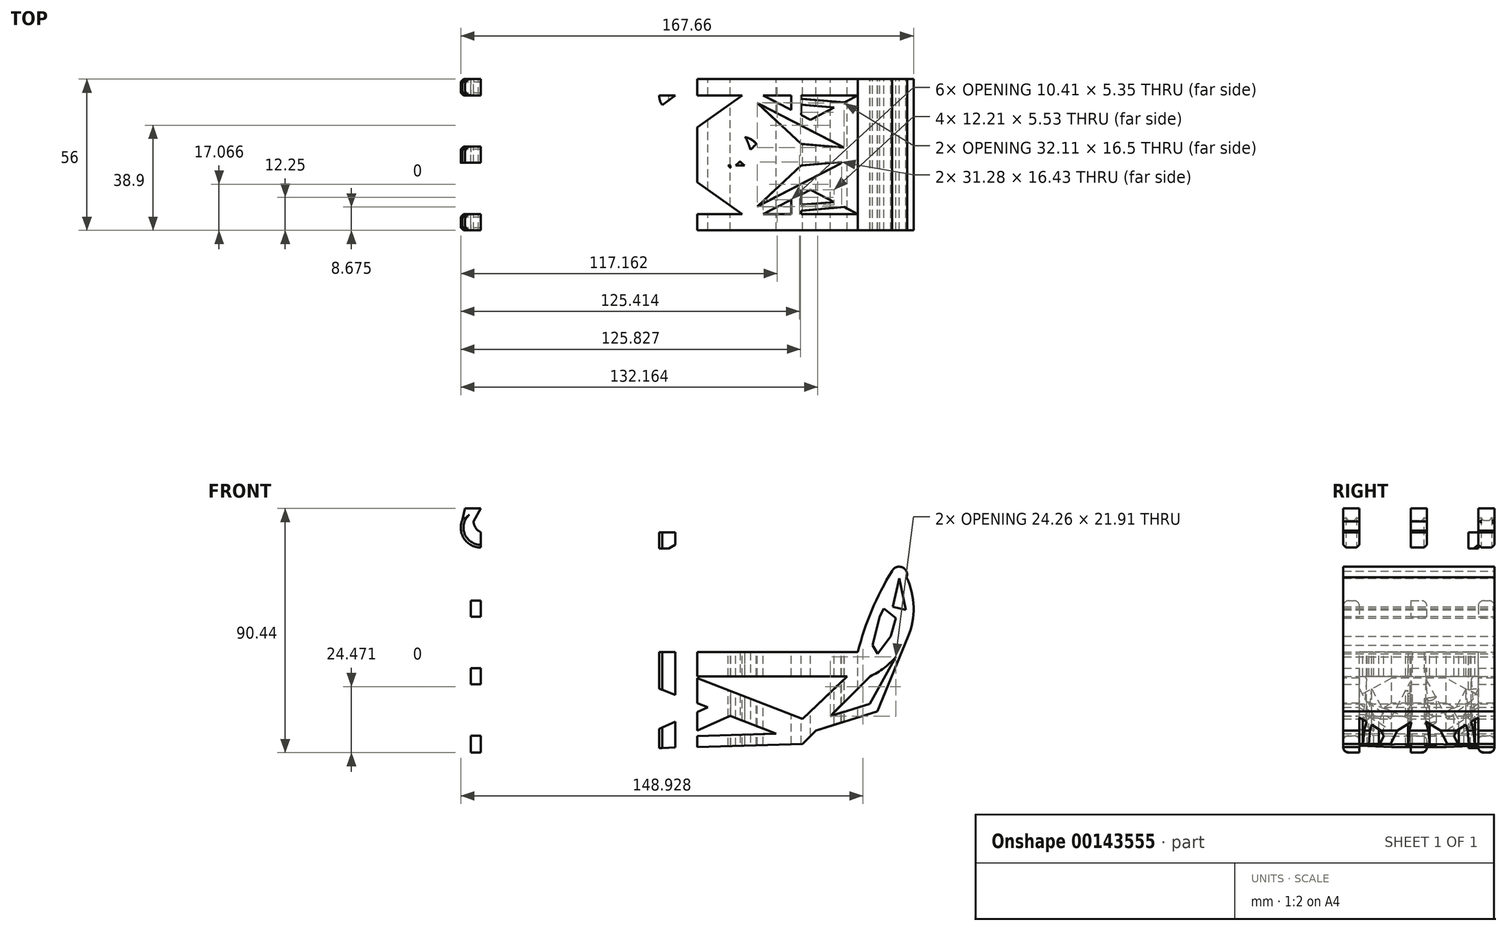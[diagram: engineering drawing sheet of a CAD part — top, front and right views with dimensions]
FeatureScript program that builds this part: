
annotation { "Feature Type Name" : "Feature", "Feature Type Description" : "" }
export const myFeature = defineFeature(function(context is Context, id is Id, definition is map)
    precondition{}
    {
        {
            var Q0;
            Q0=qCreatedBy(makeId("Front.planeOp"),FACE);
            var sketch = newSketch(context, id + "F0", { "sketchPlane" : qUnion([Q0])});
            skLineSegment(sketch, "E0.bottom", {"start": v(0, 0) * mm, "end": v(2.2, 0) * mm});
            skLineSegment(sketch, "E0.top", {"start": v(0, 6) * mm, "end": v(2.2, 6) * mm});
            skLineSegment(sketch, "E0.left", {"start": v(0, 0) * mm, "end": v(0, 6) * mm});
            skLineSegment(sketch, "E1.bottom", {"start": v(0, 6) * mm, "end": v(-4.66, 6) * mm});
            skLineSegment(sketch, "E1.top", {"start": v(0, 0.4) * mm, "end": v(-4.66, 0.4) * mm});
            skLineSegment(sketch, "E1.left", {"start": v(0, 6) * mm, "end": v(0, 0.4) * mm});
            skLineSegment(sketch, "E1.right", {"start": v(-4.66, 6) * mm, "end": v(-4.66, 0.4) * mm});
            skArc(sketch, "E2", {"start": v(-7.33, 10.05) * mm, "mid": v(-6.52, 7.68) * mm, "end": v(-4.66, 6) * mm});
            skArc(sketch, "E3", {"start": v(-11.52, 10.48) * mm, "mid": v(-10.76, 3.63) * mm, "end": v(-4.66, 0.4) * mm});
            skLineSegment(sketch, "E4", {"start": v(-4.66, 14.86) * mm, "end": v(-10.43, 14.86) * mm});
            skLineSegment(sketch, "E5", {"start": v(-10.43, 14.86) * mm, "end": v(-12, 8.6) * mm});
            skLineSegment(sketch, "E6", {"start": v(-4.66, 14.86) * mm, "end": v(-7.33, 10.05) * mm});
            skLineSegment(sketch, "E7", {"start": v(-8.25, 8.4) * mm, "end": v(-4.66, 6) * mm});
            skLineSegment(sketch, "E8.bottom", {"start": v(0, 6) * mm, "end": v(8, 6) * mm});
            skLineSegment(sketch, "E8.left", {"start": v(0, 6) * mm, "end": v(0, -7.26) * mm});
            skLineSegment(sketch, "E8.right", {"start": v(8, 6) * mm, "end": v(8, -7.26) * mm});
            skPoint(sketch, "E9.startSnap0", {"position": v(8, -0.63) * mm});
            skLineSegment(sketch, "E10.left", {"start": v(0, -7.26) * mm, "end": v(0, -22.3) * mm});
            skLineSegment(sketch, "E11", {"start": v(0, 3.2) * mm, "end": v(0, -22.3) * mm, "construction": true});
            skLineSegment(sketch, "E12.bottom", {"start": v(-8.37, -19.3) * mm, "end": v(0, -19.3) * mm});
            skLineSegment(sketch, "E12.top", {"start": v(-8.37, -25.3) * mm, "end": v(8, -25.3) * mm});
            skLineSegment(sketch, "E12.left", {"start": v(-8.37, -19.3) * mm, "end": v(-8.37, -25.3) * mm});
            skPoint(sketch, "E12.middle", {"position": v(0, -22.3) * mm});
            skLineSegment(sketch, "E13", {"start": v(8, -7.26) * mm, "end": v(8, -25.3) * mm});
            skLineSegment(sketch, "E14", {"start": v(0, -25.3) * mm, "end": v(-8.37, -25.3) * mm});
            skPoint(sketch, "E12.right.start.orphan", {"position": v(8.37, -19.3) * mm});
            skPoint(sketch, "E15.orphan", {"position": v(8.37, -25.3) * mm});
            skPoint(sketch, "E9.start.orphan", {"position": v(8, 0) * mm});
            skPoint(sketch, "E16.start.orphan", {"position": v(37.05, 0) * mm});
            skLineSegment(sketch, "E17.top", {"start": v(0, -47.3) * mm, "end": v(0.27, -47.3) * mm});
            skLineSegment(sketch, "E17.left", {"start": v(0, -22.3) * mm, "end": v(0, -38.12) * mm});
            skLineSegment(sketch, "E17.right", {"start": v(8, -22.3) * mm, "end": v(8, -38.33) * mm});
            skLineSegment(sketch, "E18.bottom", {"start": v(-8.37, -44.3) * mm, "end": v(0.18, -44.3) * mm});
            skLineSegment(sketch, "E18.top", {"start": v(-8.37, -50.3) * mm, "end": v(0.36, -50.3) * mm});
            skLineSegment(sketch, "E18.left", {"start": v(-8.37, -44.3) * mm, "end": v(-8.37, -50.3) * mm});
            skLineSegment(sketch, "E18.right", {"start": v(8.37, -47.3) * mm, "end": v(8.37, -47.46) * mm});
            skPoint(sketch, "E18.middle", {"position": v(0, -47.3) * mm});
            skLineSegment(sketch, "E19.bottom", {"start": v(8.37, -44.3) * mm, "end": v(8, -44.3) * mm});
            skLineSegment(sketch, "E19.top", {"start": v(0.36, -50.3) * mm, "end": v(-8.37, -50.3) * mm});
            skPoint(sketch, "E19.middle", {"position": v(8, -47.3) * mm});
            skPoint(sketch, "E19.right.end.orphan", {"position": v(-128, -50.3) * mm});
            skPoint(sketch, "E19.right.start.orphan", {"position": v(-119, -44.3) * mm});
            skLineSegment(sketch, "E20.bottom", {"start": v(0, 6) * mm, "end": v(75.48, 6) * mm});
            skLineSegment(sketch, "E20.left", {"start": v(0, 6) * mm, "end": v(0, 0) * mm});
            skLineSegment(sketch, "E21.bottom", {"start": v(8, -38.33) * mm, "end": v(133.63, -38.33) * mm});
            skLineSegment(sketch, "E21.left", {"start": v(8, -36.1) * mm, "end": v(8, -38.33) * mm});
            skLineSegment(sketch, "E22.bottom", {"start": v(8, -38.33) * mm, "end": v(135, -38.33) * mm});
            skLineSegment(sketch, "E22.top", {"start": v(8, -47.3) * mm, "end": v(8.37, -47.3) * mm});
            skPoint(sketch, "E23.endSnap0", {"position": v(4, -47.3) * mm});
            skLineSegment(sketch, "E24", {"start": v(4, -47.3) * mm, "end": v(4, -50.3) * mm});
            skLineSegment(sketch, "E25", {"start": v(139.5, -47.3) * mm, "end": v(114.54, -72.3) * mm});
            skLineSegment(sketch, "E26", {"start": v(104.76, -68.54) * mm, "end": v(87.68, -61.97) * mm});
            skLineSegment(sketch, "E27", {"start": v(131.03, -47.3) * mm, "end": v(114.54, -63.04) * mm});
            skLineSegment(sketch, "E28", {"start": v(114.54, -63.04) * mm, "end": v(73.6, -47.3) * mm});
            skPoint(sketch, "E29.centerSnap0", {"position": v(4, -59.8) * mm});
            skLineSegment(sketch, "E30", {"start": v(17.34, -47.3) * mm, "end": v(10.24, -53.9) * mm});
            skLineSegment(sketch, "E31", {"start": v(10.24, -53.9) * mm, "end": v(10.24, -64.47) * mm});
            skLineSegment(sketch, "E32", {"start": v(10.24, -64.47) * mm, "end": v(15, -66.9) * mm});
            skLineSegment(sketch, "E33", {"start": v(15, -66.9) * mm, "end": v(27.64, -60.68) * mm});
            skLineSegment(sketch, "E34.bottom", {"start": v(-4.5, -69.3) * mm, "end": v(4, -69.3) * mm});
            skLineSegment(sketch, "E34.top", {"start": v(-4.5, -75.3) * mm, "end": v(12.5, -75.3) * mm});
            skPoint(sketch, "E34.middle", {"position": v(4, -72.3) * mm});
            skLineSegment(sketch, "E35", {"start": v(21.25, -71) * mm, "end": v(36.6, -63.46) * mm});
            skLineSegment(sketch, "E36", {"start": v(12.5, -75.3) * mm, "end": v(114.54, -72.3) * mm});
            skPoint(sketch, "E37.end.orphan", {"position": v(4, -77.18) * mm});
            skLineSegment(sketch, "E38", {"start": v(21.25, -71) * mm, "end": v(52.02, -70.1) * mm});
            skPoint(sketch, "E39.orphan", {"position": v(135, -50.3) * mm});
            skPoint(sketch, "E19.left.start.orphan", {"position": v(144, -44.3) * mm});
            skLineSegment(sketch, "E40.trimOffspring", {"start": v(73.6, -47.3) * mm, "end": v(131.03, -47.3) * mm});
            skLineSegment(sketch, "E41", {"start": v(51.94, -55.92) * mm, "end": v(60.4, -51.48) * mm});
            skLineSegment(sketch, "E42", {"start": v(52.53, -48.45) * mm, "end": v(21.76, -47.45) * mm});
            skLineSegment(sketch, "E43", {"start": v(8.37, -47.46) * mm, "end": v(8, -47.3) * mm});
            skLineSegment(sketch, "E44", {"start": v(36.6, -63.46) * mm, "end": v(52.02, -70.1) * mm});
            skLineSegment(sketch, "E45", {"start": v(70.6, -69.54) * mm, "end": v(87.68, -61.97) * mm});
            skLineSegment(sketch, "E46", {"start": v(79.42, -58.8) * mm, "end": v(60.4, -67.23) * mm});
            skLineSegment(sketch, "E47", {"start": v(60.4, -67.23) * mm, "end": v(43.62, -60) * mm});
            skLineSegment(sketch, "E48.trimOffspring", {"start": v(43.62, -60) * mm, "end": v(51.94, -55.92) * mm});
            skPoint(sketch, "E49.end.orphan", {"position": v(60.4, -69.84) * mm});
            skPoint(sketch, "E49.start.orphan", {"position": v(82.58, -60.01) * mm});
            skLineSegment(sketch, "E50.trimOffspring", {"start": v(70.6, -69.54) * mm, "end": v(104.76, -68.54) * mm});
            skPoint(sketch, "E29.center.orphan", {"position": v(17.34, -59.8) * mm});
            skPoint(sketch, "E51.start.orphan", {"position": v(13.8, -50.6) * mm});
            skLineSegment(sketch, "E52", {"start": v(17.34, -47.3) * mm, "end": v(27.64, -60.68) * mm});
            skLineSegment(sketch, "E53", {"start": v(36.48, -56.34) * mm, "end": v(40.82, -54.2) * mm});
            skLineSegment(sketch, "E54", {"start": v(21.76, -47.45) * mm, "end": v(36.48, -56.34) * mm});
            skLineSegment(sketch, "E55.trimOffspring", {"start": v(36.48, -56.34) * mm, "end": v(52.53, -48.45) * mm});
            skArc(sketch, "E56", {"start": v(147.62, -8.33) * mm, "mid": v(140.11, -22.82) * mm, "end": v(135, -38.33) * mm});
            skArc(sketch, "E57", {"start": v(139.5, -47.3) * mm, "mid": v(144.65, -44.25) * mm, "end": v(149.02, -40.15) * mm});
            skArc(sketch, "E58", {"start": v(153.03, -10.64) * mm, "mid": v(151.41, -6.95) * mm, "end": v(147.62, -8.33) * mm});
            skLineSegment(sketch, "E59", {"start": v(150.25, -11.01) * mm, "end": v(152.71, -22.66) * mm});
            skLineSegment(sketch, "E60", {"start": v(147.92, -21.6) * mm, "end": v(152.71, -22.66) * mm});
            skLineSegment(sketch, "E61.trimOffspring", {"start": v(147.92, -21.6) * mm, "end": v(150.25, -11.01) * mm});
            skLineSegment(sketch, "E62", {"start": v(149.02, -40.15) * mm, "end": v(139.32, -57.51) * mm});
            skLineSegment(sketch, "E63", {"start": v(139.32, -57.51) * mm, "end": v(124.76, -62.06) * mm});
            skLineSegment(sketch, "E64", {"start": v(124.76, -62.06) * mm, "end": v(119.44, -67.4) * mm});
            skLineSegment(sketch, "E65", {"start": v(119.44, -67.4) * mm, "end": v(142.16, -60.29) * mm});
            skLineSegment(sketch, "E66", {"start": v(142.16, -60.29) * mm, "end": v(153.54, -32.79) * mm});
            skArc(sketch, "E67.trimOffspring", {"start": v(153.54, -32.79) * mm, "mid": v(155.61, -21.66) * mm, "end": v(153.03, -10.64) * mm});
            skLineSegment(sketch, "E68", {"start": v(143.06, -25.11) * mm, "end": v(140.34, -35.8) * mm});
            skLineSegment(sketch, "E69", {"start": v(140.34, -35.8) * mm, "end": v(142.29, -38.91) * mm});
            skLineSegment(sketch, "E70", {"start": v(142.29, -38.91) * mm, "end": v(147.14, -32.5) * mm});
            skLineSegment(sketch, "E71", {"start": v(147.14, -32.5) * mm, "end": v(149.09, -25.7) * mm});
            skLineSegment(sketch, "E72", {"start": v(149.09, -25.7) * mm, "end": v(144.62, -22.2) * mm});
            skLineSegment(sketch, "E73", {"start": v(144.62, -22.2) * mm, "end": v(143.06, -25.11) * mm});
            skPoint(sketch, "E20.right.end.orphan", {"position": v(129.94, 0) * mm});
            skLineSegment(sketch, "E74.trimOffspring", {"start": v(79.42, -58.8) * mm, "end": v(60.4, -51.48) * mm});
            skPoint(sketch, "E34.right.start.orphan", {"position": v(12.5, -69.3) * mm});
            skLineSegment(sketch, "E75", {"start": v(0, -38.12) * mm, "end": v(0.18, -44.3) * mm});
            skLineSegment(sketch, "E76", {"start": v(1.1, -75.3) * mm, "end": v(-8.37, -75.58) * mm});
            skLineSegment(sketch, "E77", {"start": v(-8.37, -75.58) * mm, "end": v(-8.37, -69.3) * mm});
            skLineSegment(sketch, "E78", {"start": v(-8.37, -69.3) * mm, "end": v(-4.5, -69.3) * mm});
            skPoint(sketch, "E79.trimOffspring.start.orphan", {"position": v(-4.5, -72.3) * mm});
            skLineSegment(sketch, "E80.trimOffspring", {"start": v(4, -69.3) * mm, "end": v(4, -72.3) * mm});
            skLineSegment(sketch, "E81.trimOffspring", {"start": v(0.18, -44.3) * mm, "end": v(-8.37, -44.3) * mm});
            skPoint(sketch, "E82.orphan", {"position": v(8.37, -50.3) * mm});
            skLineSegment(sketch, "E83.trimOffspring", {"start": v(0.36, -50.3) * mm, "end": v(0.92, -69.3) * mm});
            skLineSegment(sketch, "E84.trimOffspring", {"start": v(8, 0) * mm, "end": v(64.97, 0) * mm});
            skPoint(sketch, "E85.orphan", {"position": v(8, -19.3) * mm});
            skLineSegment(sketch, "E86", {"start": v(75.48, 6) * mm, "end": v(64.97, 0) * mm});
            skSolve(sketch);
        }
        {
            var Q0;
            Q0=qSketchRegion(id+"F0",true);
            extrude(context, id + "F1", {"entities" : qUnion([Q0]), "depth" : 5.5 * mm});
        }
        {
            var Q0;
            Q0=makeQuery(id+"F1.opExtrude","CAP_EDGE",EDGE,{"disambiguationData":[OSD([sQuery(id+"F0.wireOp",EDGE,"E12.bottom")])],"isStart":false});
            var Q1;
            Q1=makeQuery(id+"F1.opExtrude","CAP_EDGE",EDGE,{"disambiguationData":[OSD([sQuery(id+"F0.wireOp",EDGE,"E12.bottom")])],"isStart":true});
            var Q2;
            Q2=makeQuery(id+"F1.opExtrude","CAP_EDGE",EDGE,{"disambiguationData":[OSD([sQuery(id+"F0.wireOp",EDGE,"E14")])],"isStart":true});
            var Q3;
            Q3=makeQuery(id+"F1.opExtrude","CAP_EDGE",EDGE,{"disambiguationData":[OSD([sQuery(id+"F0.wireOp",EDGE,"E14")])],"isStart":false});
            fillet(context, id + "F2", {"entities" : qUnion([Q0, Q1, Q2, Q3]), "radius" : 2.66 * mm, "tangentPropagation" : true, "allowEdgeOverflow" : false});
        }
        {
            var Q0;
            Q0=makeQuery(id+"F1.opExtrude","SWEPT_EDGE",EDGE,{"disambiguationData":[OSD([sQuery(id+"F0.wireOp",EDGE,"E2"),sQuery(id+"F0.wireOp",EDGE,"E4"),sQuery(id+"F0.wireOp",EDGE,"E6")])]});
            fillet(context, id + "F3", {"entities" : qUnion([Q0]), "radius" : 1.62 * mm, "tangentPropagation" : true, "allowEdgeOverflow" : false});
        }
        {
            var Q0;
            Q0=makeQuery(id+"F1.opExtrude","CAP_EDGE",EDGE,{"disambiguationData":[OSD([sQuery(id+"F0.wireOp",EDGE,"E2")])],"isStart":true});
            var Q1;
            Q1=makeQuery(id+"F1.opExtrude","CAP_EDGE",EDGE,{"disambiguationData":[OSD([sQuery(id+"F0.wireOp",EDGE,"E2")])],"isStart":false});
            var Q2;
            Q2=makeQuery(id+"F1.opExtrude","CAP_EDGE",EDGE,{"disambiguationData":[OSD([sQuery(id+"F0.wireOp",EDGE,"E6")])],"isStart":false});
            var Q3;
            Q3=makeQuery(id+"F1.opExtrude","CAP_EDGE",EDGE,{"disambiguationData":[OSD([sQuery(id+"F0.wireOp",EDGE,"E6")])],"isStart":true});
            fillet(context, id + "F4", {"entities" : qUnion([Q0, Q1, Q2, Q3]), "radius" : .6 * mm, "tangentPropagation" : true, "allowEdgeOverflow" : false});
        }
        {
            var Q0;
            Q0=makeQuery(id+"F1.opExtrude","CAP_EDGE",EDGE,{"disambiguationData":[OSD([sQuery(id+"F0.wireOp",EDGE,"E3")])],"isStart":true});
            var Q1;
            Q1=makeQuery(id+"F1.opExtrude","CAP_EDGE",EDGE,{"disambiguationData":[OSD([sQuery(id+"F0.wireOp",EDGE,"E5")])],"isStart":true});
            var Q2;
            Q2=makeQuery(id+"F1.opExtrude","CAP_EDGE",EDGE,{"disambiguationData":[OSD([sQuery(id+"F0.wireOp",EDGE,"E1.top")])],"isStart":false});
            var Q3;
            Q3=makeQuery(id+"F1.opExtrude","CAP_EDGE",EDGE,{"disambiguationData":[OSD([sQuery(id+"F0.wireOp",EDGE,"E3")])],"isStart":false});
            var Q4;
            Q4=makeQuery(id+"F1.opExtrude","CAP_EDGE",EDGE,{"disambiguationData":[OSD([sQuery(id+"F0.wireOp",EDGE,"E5")])],"isStart":false});
            var Q5;
            Q5=makeQuery(id+"F1.opExtrude","CAP_EDGE",EDGE,{"disambiguationData":[OSD([sQuery(id+"F0.wireOp",EDGE,"E1.top")])],"isStart":true});
            fillet(context, id + "F5", {"entities" : qUnion([Q0, Q1, Q2, Q3, Q4, Q5]), "radius" : 1.49 * mm, "tangentPropagation" : true, "allowEdgeOverflow" : false});
        }
        {
            var Q0;
            Q0 = qSketchRegion(id + "F0", true);
            extrude(context, id + "F6", {"entities" : qUnion([Q0]), "operationType" : NewBodyOperationType.ADD, "depth" : 56 * mm});
        }
        {
            var Q0;
            {var subQ0=sQuery(id+"F0.wireOp",EDGE,"E76");Q0=makeQuery(id+"F6.boolean.opBoolean","MERGE",FACE,{"derivedFrom":[makeQuery(id+"F1.opExtrude","SWEPT_FACE",FACE,{"disambiguationData":[OSD([subQ0])]}),makeQuery(id+"F6.opExtrude","SWEPT_FACE",FACE,{"disambiguationData":[OSD([subQ0])]})]});}
            var sketch = newSketch(context, id + "F7", { "sketchPlane" : qUnion([Q0])});
            skLineSegment(sketch, "E87.bottom", {"start": v(-1.12, 56) * mm, "end": v(-15.4, 56) * mm});
            skLineSegment(sketch, "E87.top", {"start": v(-1.12, 0) * mm, "end": v(-15.4, 0) * mm});
            skLineSegment(sketch, "E87.left", {"start": v(-1.12, 56) * mm, "end": v(-1.12, 0) * mm});
            skLineSegment(sketch, "E87.right", {"start": v(-15.4, 56) * mm, "end": v(-15.4, 0) * mm});
            skLineSegment(sketch, "E88.top", {"start": v(-1.12, 50) * mm, "end": v(-15.4, 50) * mm});
            skLineSegment(sketch, "E88.right", {"start": v(-15.4, 56) * mm, "end": v(-15.4, 50) * mm});
            skLineSegment(sketch, "E89.top", {"start": v(-1.12, 6) * mm, "end": v(-15.4, 6) * mm});
            skLineSegment(sketch, "E89.right", {"start": v(-15.4, 0) * mm, "end": v(-15.4, 6) * mm});
            skLineSegment(sketch, "E90.top", {"start": v(-1.12, 31) * mm, "end": v(-15.4, 31) * mm});
            skLineSegment(sketch, "E90.left", {"start": v(-1.12, 28) * mm, "end": v(-1.12, 31) * mm});
            skLineSegment(sketch, "E90.right", {"start": v(-15.4, 28) * mm, "end": v(-15.4, 31) * mm});
            skLineSegment(sketch, "E91.bottom", {"start": v(-15.4, 31) * mm, "end": v(-1.12, 31) * mm});
            skLineSegment(sketch, "E91.top", {"start": v(-15.4, 25) * mm, "end": v(-1.12, 25) * mm});
            skLineSegment(sketch, "E91.left", {"start": v(-15.4, 31) * mm, "end": v(-15.4, 25) * mm});
            skSolve(sketch);
        }
        {
            var Q0;
            {var subQ0=sQuery(id+"F7.wireOp",EDGE,"E88.top");var subQ1=sQuery(id+"F7.wireOp",EDGE,"E87.left");var subQ2=makeQuery(id+"F7.imprint","INTERSECT",VERTEX,{"derivedFrom":[subQ1,subQ0]});Q0=makeQuery(id+"F7.imprint","IMPRINT",FACE,{"disambiguationData":[TD([[makeQuery(id+"F7.imprint","IMPRINT",EDGE,{"disambiguationData":[TD([[subQ2,-1.0]])],"derivedFrom":subQ1}),-1.0]])]});}
            var Q1;
            {var subQ0=sQuery(id+"F7.wireOp",EDGE,"E88.top");var subQ1=sQuery(id+"F7.wireOp",EDGE,"E87.right");var subQ2=makeQuery(id+"F7.imprint","INTERSECT",VERTEX,{"derivedFrom":[subQ1,subQ0,sQuery(id+"F7.wireOp",EDGE,"E88.right")]});Q1=makeQuery(id+"F7.imprint","IMPRINT",FACE,{"disambiguationData":[TD([[makeQuery(id+"F7.imprint","IMPRINT",EDGE,{"disambiguationData":[TD([[subQ2,-1.0]])],"derivedFrom":subQ1}),1.0]])]});}
            var Q2;
            {var subQ0=sQuery(id+"F7.wireOp",EDGE,"E89.top");var subQ1=sQuery(id+"F7.wireOp",EDGE,"E87.left");var subQ2=makeQuery(id+"F7.imprint","INTERSECT",VERTEX,{"derivedFrom":[subQ1,subQ0]});Q2=makeQuery(id+"F7.imprint","IMPRINT",FACE,{"disambiguationData":[TD([[makeQuery(id+"F7.imprint","IMPRINT",EDGE,{"disambiguationData":[TD([[subQ2,1.0]])],"derivedFrom":subQ1}),-1.0]])]});}
            var Q3;
            {var subQ0=sQuery(id+"F7.wireOp",EDGE,"E89.top");var subQ1=sQuery(id+"F7.wireOp",EDGE,"E87.right");var subQ2=makeQuery(id+"F7.imprint","INTERSECT",VERTEX,{"derivedFrom":[subQ1,subQ0,sQuery(id+"F7.wireOp",EDGE,"E89.right")]});Q3=makeQuery(id+"F7.imprint","IMPRINT",FACE,{"disambiguationData":[TD([[makeQuery(id+"F7.imprint","IMPRINT",EDGE,{"disambiguationData":[TD([[subQ2,1.0]])],"derivedFrom":subQ1}),1.0]])]});}
            extrude(context, id + "F8", {"entities" : qUnion([Q0, Q1, Q2, Q3]), "operationType" : NewBodyOperationType.REMOVE, "endBound" : BoundingType.THROUGH_ALL, "oppositeDirection" : true, "depth" : 25 * mm});
        }
        {
            var Q0;
            {var subQ0=sQuery(id+"F0.wireOp",EDGE,"E20.bottom");var subQ1=sQuery(id+"F0.wireOp",EDGE,"E1.bottom");Q0=makeQuery(id+"F6.boolean.opBoolean","MERGE",FACE,{"derivedFrom":[makeQuery(id+"F1.opExtrude","SWEPT_FACE",FACE,{"disambiguationData":[OSD([subQ1,subQ0])]}),makeQuery(id+"F6.opExtrude","SWEPT_FACE",FACE,{"disambiguationData":[OSD([subQ1,subQ0])]})]});}
            var sketch = newSketch(context, id + "F9", { "sketchPlane" : qUnion([Q0])});
            skLineSegment(sketch, "E92.top", {"start": v(15.03, -50) * mm, "end": v(39.96, -50) * mm});
            skLineSegment(sketch, "E93", {"start": v(12.55, -9.31) * mm, "end": v(7.82, -15.65) * mm});
            skLineSegment(sketch, "E94", {"start": v(7.82, -15.65) * mm, "end": v(15.03, -24.07) * mm});
            skPoint(sketch, "E94.endSnap0", {"position": v(7.82, -28) * mm});
            skLineSegment(sketch, "E95", {"start": v(15.03, -31.97) * mm, "end": v(7.82, -40.5) * mm});
            skPoint(sketch, "E95.endSnap0", {"position": v(-1.3, -40.5) * mm});
            skLineSegment(sketch, "E96", {"start": v(7.82, -40.5) * mm, "end": v(12.53, -46.7) * mm});
            skPoint(sketch, "E97.orphan", {"position": v(7.82, -6) * mm});
            skPoint(sketch, "E98.orphan", {"position": v(7.82, -50) * mm});
            skLineSegment(sketch, "E99", {"start": v(15.03, -6) * mm, "end": v(40.59, -6) * mm});
            skLineSegment(sketch, "E100", {"start": v(69.45, -6) * mm, "end": v(66.07, -12.15) * mm});
            skPoint(sketch, "E100.endSnap0", {"position": v(15.03, -15.04) * mm});
            skLineSegment(sketch, "E101", {"start": v(64.61, -15.53) * mm, "end": v(66.79, -24.07) * mm});
            skLineSegment(sketch, "E102", {"start": v(66.74, -31.97) * mm, "end": v(64.49, -40.5) * mm});
            skLineSegment(sketch, "E103", {"start": v(40.86, -6.91) * mm, "end": v(27.3, -15.92) * mm});
            skLineSegment(sketch, "E104", {"start": v(43.56, -6.98) * mm, "end": v(54.86, -15.3) * mm});
            skLineSegment(sketch, "E105", {"start": v(40.21, -49.18) * mm, "end": v(27.11, -40.23) * mm});
            skLineSegment(sketch, "E106", {"start": v(42.59, -49.16) * mm, "end": v(54.67, -40.56) * mm});
            skPoint(sketch, "E92.right.start.orphan", {"position": v(67.79, -6) * mm});
            skLineSegment(sketch, "E107", {"start": v(69.45, -50) * mm, "end": v(66.22, -43.81) * mm});
            skLineSegment(sketch, "E108", {"start": v(18.38, -28) * mm, "end": v(28.6, -21.22) * mm});
            skLineSegment(sketch, "E109", {"start": v(42.24, -12.16) * mm, "end": v(50.7, -18.38) * mm});
            skLineSegment(sketch, "E110", {"start": v(63.76, -28) * mm, "end": v(52.31, -36.15) * mm});
            skLineSegment(sketch, "E111", {"start": v(41.4, -43.9) * mm, "end": v(31.25, -36.89) * mm});
            skLineSegment(sketch, "E112", {"start": v(15.03, -6) * mm, "end": v(27.3, -15.92) * mm});
            skLineSegment(sketch, "E113", {"start": v(69.45, -6) * mm, "end": v(63.55, -10.77) * mm});
            skLineSegment(sketch, "E114.right", {"start": v(45.24, -25) * mm, "end": v(45.24, -25.57) * mm});
            skPoint(sketch, "E114.middle", {"position": v(42.24, -28) * mm});
            skLineSegment(sketch, "E115.trimOffspring", {"start": v(31.48, -19.3) * mm, "end": v(38.63, -25.09) * mm});
            skLineSegment(sketch, "E116.trimOffspring", {"start": v(52.5, -19.7) * mm, "end": v(43.24, -27.2) * mm});
            skLineSegment(sketch, "E117", {"start": v(12.55, -9.31) * mm, "end": v(24.22, -17.97) * mm});
            skLineSegment(sketch, "E118", {"start": v(75.48, -56) * mm, "end": v(0, -56) * mm});
            skLineSegment(sketch, "E119", {"start": v(12.53, -46.7) * mm, "end": v(24.06, -38.15) * mm});
            skLineSegment(sketch, "E120.trimOffspring", {"start": v(28.6, -21.22) * mm, "end": v(36.9, -27.37) * mm});
            skLineSegment(sketch, "E121.trimOffspring", {"start": v(28.4, -34.92) * mm, "end": v(36.9, -28.63) * mm});
            skLineSegment(sketch, "E122", {"start": v(15.03, -50) * mm, "end": v(27.11, -40.23) * mm});
            skLineSegment(sketch, "E123.trimOffspring", {"start": v(45.24, -30.43) * mm, "end": v(52.31, -36.15) * mm});
            skLineSegment(sketch, "E124.trimOffspring", {"start": v(41.61, -25.13) * mm, "end": v(50.7, -18.38) * mm});
            skLineSegment(sketch, "E125.trimOffspring", {"start": v(41.61, -30.87) * mm, "end": v(50.48, -37.45) * mm});
            skPoint(sketch, "E126.orphan", {"position": v(39.24, -28) * mm});
            skLineSegment(sketch, "E127.trimOffspring", {"start": v(43.24, -28.8) * mm, "end": v(52.31, -36.15) * mm});
            skLineSegment(sketch, "E128.trimOffspring", {"start": v(43.24, -27.2) * mm, "end": v(52.5, -19.7) * mm});
            skLineSegment(sketch, "E129.trimOffspring", {"start": v(52.5, -19.7) * mm, "end": v(63.76, -28) * mm});
            skLineSegment(sketch, "E130.trimOffspring", {"start": v(56.48, -16.48) * mm, "end": v(66.79, -24.07) * mm});
            skLineSegment(sketch, "E131.trimOffspring", {"start": v(56.32, -39.39) * mm, "end": v(60.64, -42.88) * mm});
            skLineSegment(sketch, "E132.trimOffspring", {"start": v(54.67, -40.56) * mm, "end": v(59.55, -44.18) * mm});
            skLineSegment(sketch, "E133.trimOffspring", {"start": v(31.25, -36.89) * mm, "end": v(38.63, -30.91) * mm});
            skLineSegment(sketch, "E134.trimOffspring", {"start": v(31.48, -19.3) * mm, "end": v(39.24, -25.57) * mm});
            skPoint(sketch, "E135.end.orphan", {"position": v(45.24, -28) * mm});
            skLineSegment(sketch, "E136.trimOffspring", {"start": v(45.24, -30.43) * mm, "end": v(45.24, -31) * mm});
            skLineSegment(sketch, "E137.trimOffspring", {"start": v(56.32, -39.39) * mm, "end": v(66.74, -31.97) * mm});
            skLineSegment(sketch, "E138.trimOffspring", {"start": v(50.48, -37.45) * mm, "end": v(41.4, -43.9) * mm});
            skLineSegment(sketch, "E139.trimOffspring", {"start": v(31.48, -19.3) * mm, "end": v(42.24, -12.16) * mm});
            skLineSegment(sketch, "E140.trimOffspring", {"start": v(24.22, -17.97) * mm, "end": v(15.03, -24.07) * mm});
            skLineSegment(sketch, "E141.trimOffspring", {"start": v(54.86, -15.3) * mm, "end": v(59.55, -11.82) * mm});
            skLineSegment(sketch, "E142.trimOffspring", {"start": v(56.48, -16.48) * mm, "end": v(60.64, -13.12) * mm});
            skPoint(sketch, "E143.orphan", {"position": v(67.79, -50) * mm});
            skPoint(sketch, "E144.orphan", {"position": v(67.79, -28) * mm});
            skArc(sketch, "E145", {"start": v(42.86, -50) * mm, "mid": v(42.79, -49.56) * mm, "end": v(42.59, -49.16) * mm});
            skArc(sketch, "E146", {"start": v(40.59, -6) * mm, "mid": v(40.66, -6.48) * mm, "end": v(40.86, -6.91) * mm});
            skPoint(sketch, "E147.trimOffspring.end.orphan", {"position": v(39.24, -31) * mm});
            skLineSegment(sketch, "E148.trimOffspring", {"start": v(38.63, -30.91) * mm, "end": v(31.25, -36.89) * mm});
            skArc(sketch, "E149", {"start": v(36.9, -27.37) * mm, "mid": v(36.83, -28) * mm, "end": v(36.9, -28.63) * mm});
            skLineSegment(sketch, "E150.trimOffspring", {"start": v(43.89, -6) * mm, "end": v(57.7, -6) * mm});
            skArc(sketch, "E151.trimOffspring", {"start": v(43.56, -6.98) * mm, "mid": v(43.8, -6.51) * mm, "end": v(43.89, -6) * mm});
            skArc(sketch, "E152.trimOffspring", {"start": v(40.21, -49.18) * mm, "mid": v(40.03, -49.57) * mm, "end": v(39.96, -50) * mm});
            skLineSegment(sketch, "E153.trimOffspring", {"start": v(42.86, -50) * mm, "end": v(67.4, -50) * mm});
            skArc(sketch, "E154.trimOffspring", {"start": v(38.63, -30.91) * mm, "mid": v(40.13, -31.25) * mm, "end": v(41.61, -30.87) * mm});
            skArc(sketch, "E155.trimOffspring", {"start": v(43.24, -28.8) * mm, "mid": v(43.34, -28) * mm, "end": v(43.24, -27.2) * mm});
            skPoint(sketch, "E156.orphan", {"position": v(40.08, -29.74) * mm});
            skArc(sketch, "E157.trimOffspring", {"start": v(41.61, -25.13) * mm, "mid": v(40.13, -24.75) * mm, "end": v(38.63, -25.09) * mm});
            skPoint(sketch, "E114.left.start.orphan", {"position": v(39.24, -25) * mm});
            skArc(sketch, "E158", {"start": v(64.5, -40.47) * mm, "mid": v(62.43, -41.45) * mm, "end": v(60.64, -42.88) * mm});
            skArc(sketch, "E159", {"start": v(66.22, -43.81) * mm, "mid": v(64.8, -44.36) * mm, "end": v(63.55, -45.23) * mm});
            skLineSegment(sketch, "E160", {"start": v(40.08, -28) * mm, "end": v(80.79, -28) * mm, "construction": true});
            skArc(sketch, "E161.trimOffspring", {"start": v(59.55, -44.18) * mm, "mid": v(58.18, -46.95) * mm, "end": v(57.7, -50) * mm});
            skLineSegment(sketch, "E162.trimOffspring", {"start": v(63.55, -45.23) * mm, "end": v(69.45, -50) * mm});
            skLineSegment(sketch, "E163.trimOffspring", {"start": v(62.52, -46.39) * mm, "end": v(67.4, -50) * mm});
            skArc(sketch, "E164.trimOffspring", {"start": v(62.52, -46.39) * mm, "mid": v(61.7, -48.11) * mm, "end": v(61.4, -50) * mm});
            skArc(sketch, "E165.MirrorCS", {"start": v(62.52, -9.61) * mm, "mid": v(61.7, -7.89) * mm, "end": v(61.4, -6) * mm});
            skArc(sketch, "E166.MirrorCS", {"start": v(59.55, -11.82) * mm, "mid": v(58.18, -9.05) * mm, "end": v(57.7, -6) * mm});
            skArc(sketch, "E167.MirrorCS", {"start": v(64.5, -15.53) * mm, "mid": v(62.43, -14.55) * mm, "end": v(60.64, -13.12) * mm});
            skArc(sketch, "E168.MirrorCS", {"start": v(66.22, -12.19) * mm, "mid": v(64.8, -11.64) * mm, "end": v(63.55, -10.77) * mm});
            skLineSegment(sketch, "E169.trimOffspring", {"start": v(24.06, -38.15) * mm, "end": v(15.03, -31.97) * mm});
            skLineSegment(sketch, "E170.trimOffspring", {"start": v(28.4, -34.92) * mm, "end": v(18.38, -28) * mm});
            skLineSegment(sketch, "E171.trimOffspring", {"start": v(62.52, -9.61) * mm, "end": v(67.4, -6) * mm});
            skLineSegment(sketch, "E172.trimOffspring", {"start": v(63.55, -10.77) * mm, "end": v(69.45, -6) * mm});
            skLineSegment(sketch, "E173.trimOffspring", {"start": v(60.64, -13.12) * mm, "end": v(56.48, -16.48) * mm});
            skLineSegment(sketch, "E174.trimOffspring", {"start": v(61.4, -6) * mm, "end": v(67.79, -6) * mm});
            skLineSegment(sketch, "E175", {"start": v(64.5, -15.53) * mm, "end": v(64.61, -15.53) * mm});
            skPoint(sketch, "E176.orphan", {"position": v(64.49, -15.04) * mm});
            skSolve(sketch);
        }
        {
            var Q0;
            Q0=makeQuery(id+"F9.imprint","IMPRINT",FACE,{"disambiguationData":[TD([[makeQuery(id+"F9.imprint","IMPRINT",EDGE,{"derivedFrom":sQuery(id+"F9.wireOp",EDGE,"E109")}),-1.0]])]});
            var Q1;
            Q1=makeQuery(id+"F9.imprint","IMPRINT",FACE,{"disambiguationData":[TD([[makeQuery(id+"F9.imprint","IMPRINT",EDGE,{"derivedFrom":sQuery(id+"F9.wireOp",EDGE,"E111")}),-1.0]])]});
            var Q2;
            Q2=makeQuery(id+"F9.imprint","IMPRINT",FACE,{"disambiguationData":[TD([[makeQuery(id+"F9.imprint","IMPRINT",EDGE,{"derivedFrom":sQuery(id+"F9.wireOp",EDGE,"E108")}),-1.0]])]});
            var Q3;
            Q3=makeQuery(id+"F9.imprint","IMPRINT",FACE,{"disambiguationData":[TD([[makeQuery(id+"F9.imprint","IMPRINT",EDGE,{"derivedFrom":sQuery(id+"F9.wireOp",EDGE,"E93")}),1.0]])]});
            var Q4;
            Q4=makeQuery(id+"F9.imprint","IMPRINT",FACE,{"disambiguationData":[TD([[makeQuery(id+"F9.imprint","IMPRINT",EDGE,{"derivedFrom":sQuery(id+"F9.wireOp",EDGE,"E99")}),-1.0]])]});
            var Q5;
            Q5=makeQuery(id+"F9.imprint","IMPRINT",FACE,{"disambiguationData":[TD([[makeQuery(id+"F9.imprint","IMPRINT",EDGE,{"derivedFrom":sQuery(id+"F9.wireOp",EDGE,"E104")}),1.0]])]});
            var Q6;
            {var subQ0=sQuery(id+"F9.wireOp",EDGE,"E165.MirrorCS");Q6=makeQuery(id+"F9.imprint","IMPRINT",FACE,{"disambiguationData":[TD([[makeQuery(id+"F9.imprint","IMPRINT",EDGE,{"derivedFrom":subQ0}),-1.0]])]});}
            var Q7;
            {var subQ0=sQuery(id+"F9.wireOp",EDGE,"E100");Q7=makeQuery(id+"F9.imprint","IMPRINT",FACE,{"disambiguationData":[TD([[makeQuery(id+"F9.imprint","IMPRINT",EDGE,{"derivedFrom":subQ0}),-1.0]])]});}
            var Q8;
            Q8=makeQuery(id+"F9.imprint","IMPRINT",FACE,{"disambiguationData":[TD([[makeQuery(id+"F9.imprint","IMPRINT",EDGE,{"derivedFrom":sQuery(id+"F9.wireOp",EDGE,"E101")}),-1.0]])]});
            var Q9;
            {var subQ4=sQuery(id+"F9.wireOp",EDGE,"E110");Q9=makeQuery(id+"F9.imprint","IMPRINT",FACE,{"disambiguationData":[TD([[makeQuery(id+"F9.imprint","IMPRINT",EDGE,{"derivedFrom":subQ4}),-1.0]])]});}
            var Q10;
            Q10=makeQuery(id+"F9.imprint","IMPRINT",FACE,{"disambiguationData":[TD([[makeQuery(id+"F9.imprint","IMPRINT",EDGE,{"derivedFrom":sQuery(id+"F9.wireOp",EDGE,"E131.trimOffspring")}),1.0]])]});
            var Q11;
            Q11=makeQuery(id+"F9.imprint","IMPRINT",FACE,{"disambiguationData":[TD([[makeQuery(id+"F9.imprint","IMPRINT",EDGE,{"derivedFrom":sQuery(id+"F9.wireOp",EDGE,"E107")}),1.0]])]});
            var Q12;
            {var subQ0=sQuery(id+"F9.wireOp",EDGE,"E163.trimOffspring");Q12=makeQuery(id+"F9.imprint","IMPRINT",FACE,{"disambiguationData":[TD([[makeQuery(id+"F9.imprint","IMPRINT",EDGE,{"derivedFrom":subQ0}),-1.0]])]});}
            var Q13;
            Q13=makeQuery(id+"F9.imprint","IMPRINT",FACE,{"disambiguationData":[TD([[makeQuery(id+"F9.imprint","IMPRINT",EDGE,{"derivedFrom":sQuery(id+"F9.wireOp",EDGE,"E106")}),-1.0]])]});
            var Q14;
            Q14=makeQuery(id+"F9.imprint","IMPRINT",FACE,{"disambiguationData":[TD([[makeQuery(id+"F9.imprint","IMPRINT",EDGE,{"derivedFrom":sQuery(id+"F9.wireOp",EDGE,"E92.top")}),1.0]])]});
            var Q15;
            Q15=makeQuery(id+"F9.imprint","IMPRINT",FACE,{"disambiguationData":[TD([[makeQuery(id+"F9.imprint","IMPRINT",EDGE,{"derivedFrom":sQuery(id+"F9.wireOp",EDGE,"E95")}),1.0]])]});
            extrude(context, id + "F10", {"entities" : qUnion([Q0, Q1, Q2, Q3, Q4, Q5, Q6, Q7, Q8, Q9, Q10, Q11, Q12, Q13, Q14, Q15]), "operationType" : NewBodyOperationType.REMOVE, "endBound" : BoundingType.THROUGH_ALL, "oppositeDirection" : true, "depth" : 25 * mm});
        }
        {
            var Q0;
            {var subQ0=sQuery(id+"F0.wireOp",EDGE,"E22.bottom");Q0=makeQuery(id+"F6.boolean.opBoolean","MERGE",FACE,{"derivedFrom":[makeQuery(id+"F1.opExtrude","SWEPT_FACE",FACE,{"disambiguationData":[OSD([subQ0])]}),makeQuery(id+"F6.opExtrude","SWEPT_FACE",FACE,{"disambiguationData":[OSD([subQ0])]})]});}
            var sketch = newSketch(context, id + "F11", { "sketchPlane" : qUnion([Q0])});
            skLineSegment(sketch, "E177.bottom", {"start": v(69.34, -31.97) * mm, "end": v(69.45, -31.97) * mm});
            skLineSegment(sketch, "E177.top", {"start": v(66.74, -24.03) * mm, "end": v(66.85, -24.03) * mm});
            skLineSegment(sketch, "E177.left", {"start": v(66.74, -30.12) * mm, "end": v(66.74, -25.88) * mm});
            skPoint(sketch, "E177.middle", {"position": v(135, -28) * mm});
            skLineSegment(sketch, "E178.bottom", {"start": v(72.46, -6) * mm, "end": v(92.19, -6) * mm});
            skLineSegment(sketch, "E178.top", {"start": v(72.46, -50) * mm, "end": v(92.19, -50) * mm});
            skLineSegment(sketch, "E178.left", {"start": v(69.45, -6) * mm, "end": v(69.45, -22.18) * mm});
            skLineSegment(sketch, "E178.right", {"start": v(135, -6) * mm, "end": v(135, -8.5) * mm});
            skLineSegment(sketch, "E179", {"start": v(66.79, -24.07) * mm, "end": v(66.85, -24.03) * mm});
            skLineSegment(sketch, "E180", {"start": v(92.19, -6) * mm, "end": v(129.84, -25.35) * mm});
            skLineSegment(sketch, "E181", {"start": v(129.84, -30.65) * mm, "end": v(92.19, -50) * mm});
            skLineSegment(sketch, "E182", {"start": v(92.19, -50) * mm, "end": v(72.46, -36.03) * mm});
            skArc(sketch, "E183", {"start": v(92.14, -21.44) * mm, "mid": v(89.19, -22.17) * mm, "end": v(86.88, -24.15) * mm});
            skFitSpline(sketch, "E184.trimOffspring", {"points": [v(92.19, -28) * mm, v(97.4, -24.03) * mm, v(87.93, -32.99) * mm, v(90.96, -27) * mm, v(92.19, -28) * mm]});
            skLineSegment(sketch, "E185.trimOffspring", {"start": v(96.44, -31.97) * mm, "end": v(101.02, -31.97) * mm});
            skLineSegment(sketch, "E186.trimOffspring", {"start": v(91.34, -30.5) * mm, "end": v(91.34, -30.5) * mm});
            skCircle(sketch, "E187", {"center": v(92.19, -28) * mm, "radius": 9.69 * mm});
            skArc(sketch, "E188.trimOffspring", {"start": v(86.45, -24.82) * mm, "mid": v(86.45, -24.82) * mm, "end": v(86.45, -24.82) * mm});
            skFitSpline(sketch, "E189.trimOffspring", {"points": [v(93.14, -21.51) * mm, v(92.19, -28) * mm, v(86.45, -24.82) * mm, v(95.97, -33.36) * mm, v(93.14, -21.51) * mm]});
            skArc(sketch, "E190.trimOffspring", {"start": v(86.1, -25.54) * mm, "mid": v(95, -33.92) * mm, "end": v(94.1, -21.73) * mm});
            skLineSegment(sketch, "E191.bottom", {"start": v(72.46, -24.03) * mm, "end": v(79.71, -24.03) * mm});
            skLineSegment(sketch, "E191.top", {"start": v(72.46, -31.97) * mm, "end": v(79.71, -31.97) * mm});
            skLineSegment(sketch, "E191.left", {"start": v(69.45, -24.03) * mm, "end": v(69.45, -31.97) * mm});
            skPoint(sketch, "E191.middle", {"position": v(91.73, -28) * mm});
            skPoint(sketch, "E191.middle.positionSnap0", {"position": v(69.45, -28) * mm});
            skPoint(sketch, "E191.cornerSnap0", {"position": v(69.45, -28) * mm});
            skPoint(sketch, "E191.centerSnap0", {"position": v(69.45, -28) * mm});
            skLineSegment(sketch, "E192", {"start": v(66.74, -25.88) * mm, "end": v(69.45, -23.95) * mm});
            skLineSegment(sketch, "E193", {"start": v(97.73, -8.85) * mm, "end": v(114.02, -24.03) * mm});
            skLineSegment(sketch, "E194", {"start": v(114.02, -31.97) * mm, "end": v(97.73, -47.15) * mm});
            skLineSegment(sketch, "E195", {"start": v(135, -31.97) * mm, "end": v(114.02, -42.75) * mm});
            skPoint(sketch, "E195.endSnap0", {"position": v(102.22, -50) * mm});
            skLineSegment(sketch, "E196", {"start": v(99.92, -50) * mm, "end": v(110.33, -44.65) * mm});
            skLineSegment(sketch, "E197", {"start": v(135, -24.03) * mm, "end": v(114.02, -13.25) * mm});
            skLineSegment(sketch, "E198.trimOffspring", {"start": v(69.45, -23.95) * mm, "end": v(69.45, -32.05) * mm, "construction": true});
            skLineSegment(sketch, "E199.trimOffspring", {"start": v(69.45, -33.9) * mm, "end": v(69.45, -53.04) * mm, "construction": true});
            skLineSegment(sketch, "E200.trimOffspring", {"start": v(69.45, -33.9) * mm, "end": v(69.45, -50) * mm});
            skLineSegment(sketch, "E201.trimOffspring", {"start": v(69.45, -32.05) * mm, "end": v(66.74, -30.12) * mm});
            skLineSegment(sketch, "E202.trimOffspring", {"start": v(69.45, -23.95) * mm, "end": v(69.45, -32.05) * mm});
            skLineSegment(sketch, "E203.trimOffspring", {"start": v(69.34, -24.03) * mm, "end": v(69.45, -24.03) * mm});
            skLineSegment(sketch, "E204.trimOffspring", {"start": v(72.46, -20.04) * mm, "end": v(92.19, -6) * mm});
            skLineSegment(sketch, "E205", {"start": v(129.84, -25.35) * mm, "end": v(114.02, -24.03) * mm});
            skLineSegment(sketch, "E206", {"start": v(114.02, -31.97) * mm, "end": v(129.84, -30.65) * mm});
            skLineSegment(sketch, "E207", {"start": v(117.46, -15.01) * mm, "end": v(126.23, -10.5) * mm});
            skLineSegment(sketch, "E208", {"start": v(117.46, -40.99) * mm, "end": v(126.23, -45.5) * mm});
            skLineSegment(sketch, "E209", {"start": v(126.23, -45.5) * mm, "end": v(114.02, -46.51) * mm});
            skLineSegment(sketch, "E210", {"start": v(114.02, -46.51) * mm, "end": v(114.02, -42.75) * mm});
            skLineSegment(sketch, "E211", {"start": v(114.02, -42.75) * mm, "end": v(114.02, -46.51) * mm});
            skLineSegment(sketch, "E212", {"start": v(114.02, -50) * mm, "end": v(114.02, -48.72) * mm});
            skLineSegment(sketch, "E213", {"start": v(110.33, -6) * mm, "end": v(110.33, -11.35) * mm});
            skLineSegment(sketch, "E214.trimOffspring", {"start": v(110.33, -44.65) * mm, "end": v(110.33, -50) * mm});
            skLineSegment(sketch, "E215.trimOffspring", {"start": v(114.02, -42.75) * mm, "end": v(135, -31.97) * mm});
            skLineSegment(sketch, "E216.trimOffspring", {"start": v(114.02, -50) * mm, "end": v(135, -50) * mm});
            skLineSegment(sketch, "E217.trimOffspring", {"start": v(114.02, -13.25) * mm, "end": v(114.02, -9.49) * mm});
            skLineSegment(sketch, "E218.trimOffspring", {"start": v(110.33, -11.35) * mm, "end": v(99.92, -6) * mm});
            skLineSegment(sketch, "E219", {"start": v(126.23, -10.5) * mm, "end": v(114.02, -9.49) * mm});
            skLineSegment(sketch, "E220.trimOffspring", {"start": v(99.92, -6) * mm, "end": v(110.33, -6) * mm});
            skPoint(sketch, "E221.orphan", {"position": v(94.67, -50) * mm});
            skLineSegment(sketch, "E222.trimOffspring", {"start": v(99.92, -50) * mm, "end": v(110.33, -50) * mm});
            skLineSegment(sketch, "E223.trimOffspring", {"start": v(110.33, -44.65) * mm, "end": v(99.92, -50) * mm});
            skLineSegment(sketch, "E224.trimOffspring", {"start": v(114.02, -6) * mm, "end": v(135, -6) * mm});
            skLineSegment(sketch, "E225", {"start": v(114.02, -7.28) * mm, "end": v(129.92, -8.6) * mm});
            skLineSegment(sketch, "E226", {"start": v(114.02, -48.72) * mm, "end": v(130.73, -47.33) * mm});
            skPoint(sketch, "E226.endSnap0", {"position": v(105.12, -47.33) * mm});
            skLineSegment(sketch, "E227.trimOffspring", {"start": v(129.92, -8.6) * mm, "end": v(135, -6) * mm});
            skLineSegment(sketch, "E228.trimOffspring", {"start": v(114.02, -7.28) * mm, "end": v(114.02, -6) * mm});
            skLineSegment(sketch, "E229.trimOffspring", {"start": v(129.92, -47.4) * mm, "end": v(135, -50) * mm});
            skLineSegment(sketch, "E230.trimOffspring", {"start": v(114.02, -48.72) * mm, "end": v(114.02, -50) * mm});
            skLineSegment(sketch, "E231", {"start": v(122.34, -15.01) * mm, "end": v(133.08, -9.5) * mm});
            skLineSegment(sketch, "E232", {"start": v(133.08, -9.5) * mm, "end": v(122.34, -15.01) * mm});
            skLineSegment(sketch, "E233", {"start": v(122.34, -15.01) * mm, "end": v(133.08, -20.54) * mm});
            skLineSegment(sketch, "E234", {"start": v(122.34, -40.99) * mm, "end": v(133.08, -35.46) * mm});
            skLineSegment(sketch, "E235", {"start": v(133.08, -35.46) * mm, "end": v(122.34, -40.99) * mm});
            skLineSegment(sketch, "E236", {"start": v(122.34, -40.99) * mm, "end": v(133.08, -46.5) * mm});
            skLineSegment(sketch, "E237.trimOffspring", {"start": v(129.02, -30.72) * mm, "end": v(128.67, -31.25) * mm});
            skLineSegment(sketch, "E238.trimOffspring", {"start": v(135, -47.5) * mm, "end": v(135, -50) * mm});
            skLineSegment(sketch, "E239.trimOffspring", {"start": v(135, -21.52) * mm, "end": v(135, -34.48) * mm});
            skLineSegment(sketch, "E240", {"start": v(133.08, -9.5) * mm, "end": v(133.08, -20.54) * mm});
            skLineSegment(sketch, "E241", {"start": v(133.08, -35.46) * mm, "end": v(133.08, -46.5) * mm});
            skPoint(sketch, "E242.orphan", {"position": v(94.67, -7.28) * mm});
            skPoint(sketch, "E243.trimOffspring.end.orphan", {"position": v(94.67, -48.72) * mm});
            skPoint(sketch, "E177.right.end.orphan", {"position": v(203.26, -24.03) * mm});
            skPoint(sketch, "E177.right.start.orphan", {"position": v(203.26, -31.97) * mm});
            skLineSegment(sketch, "E244.trimOffspring", {"start": v(97.39, -24.03) * mm, "end": v(97.4, -24.03) * mm});
            skCircle(sketch, "E245", {"center": v(92.19, -28) * mm, "radius": 6.55 * mm});
            skLineSegment(sketch, "E246", {"start": v(72.46, -6) * mm, "end": v(72.46, -20.04) * mm});
            skLineSegment(sketch, "E247", {"start": v(72.46, -24.03) * mm, "end": v(72.46, -31.97) * mm});
            skLineSegment(sketch, "E248", {"start": v(79.71, -24.03) * mm, "end": v(79.71, -31.97) * mm});
            skLineSegment(sketch, "E249", {"start": v(79.71, -31.97) * mm, "end": v(72.46, -31.97) * mm});
            skPoint(sketch, "E250.startSnap0", {"position": v(79.71, -28) * mm});
            skLineSegment(sketch, "E251", {"start": v(107.47, -28) * mm, "end": v(102.32, -37.58) * mm});
            skLineSegment(sketch, "E252", {"start": v(102.32, -37.58) * mm, "end": v(115.04, -28) * mm});
            skLineSegment(sketch, "E253", {"start": v(115.04, -28) * mm, "end": v(102.32, -21.15) * mm});
            skLineSegment(sketch, "E254", {"start": v(107.47, -28) * mm, "end": v(102.32, -21.15) * mm});
            skPoint(sketch, "E255.orphan", {"position": v(119.48, -28) * mm});
            skLineSegment(sketch, "E256.trimOffspring", {"start": v(72.46, -36.03) * mm, "end": v(72.46, -50) * mm});
            skLineSegment(sketch, "E257.trimOffspring", {"start": v(69.45, -33.9) * mm, "end": v(66.74, -31.97) * mm});
            skLineSegment(sketch, "E258.trimOffspring", {"start": v(83.35, -31.97) * mm, "end": v(86.97, -31.97) * mm});
            skLineSegment(sketch, "E259.trimOffspring", {"start": v(83.35, -24.03) * mm, "end": v(86.97, -24.03) * mm});
            skLineSegment(sketch, "E260.trimOffspring", {"start": v(83.35, -31.97) * mm, "end": v(97.4, -31.97) * mm});
            skLineSegment(sketch, "E261", {"start": v(83.35, -24.03) * mm, "end": v(101.02, -24.03) * mm});
            skSolve(sketch);
        }
        {
            var Q0;
            {var subQ2=sQuery(id+"F11.wireOp",EDGE,"E193");Q0=makeQuery(id+"F11.imprint","IMPRINT",FACE,{"disambiguationData":[TD([[makeQuery(id+"F11.imprint","IMPRINT",EDGE,{"derivedFrom":subQ2}),1.0]])]});}
            var Q1;
            {var subQ0=sQuery(id+"F11.wireOp",EDGE,"E194");Q1=makeQuery(id+"F11.imprint","IMPRINT",FACE,{"disambiguationData":[TD([[makeQuery(id+"F11.imprint","IMPRINT",EDGE,{"derivedFrom":subQ0}),1.0]])]});}
            var Q2;
            Q2=makeQuery(id+"F11.imprint","IMPRINT",FACE,{"disambiguationData":[TD([[makeQuery(id+"F11.imprint","IMPRINT",EDGE,{"derivedFrom":sQuery(id+"F11.wireOp",EDGE,"E235")}),1.0]])]});
            var Q3;
            Q3=makeQuery(id+"F11.imprint","IMPRINT",FACE,{"disambiguationData":[TD([[makeQuery(id+"F11.imprint","IMPRINT",EDGE,{"derivedFrom":sQuery(id+"F11.wireOp",EDGE,"E232")}),1.0]])]});
            var Q4;
            Q4=makeQuery(id+"F11.imprint","IMPRINT",FACE,{"disambiguationData":[TD([[makeQuery(id+"F11.imprint","IMPRINT",EDGE,{"derivedFrom":sQuery(id+"F11.wireOp",EDGE,"E224.trimOffspring")}),-1.0]])]});
            var Q5;
            {var subQ2=sQuery(id+"F11.wireOp",EDGE,"E207");Q5=makeQuery(id+"F11.imprint","IMPRINT",FACE,{"disambiguationData":[TD([[makeQuery(id+"F11.imprint","IMPRINT",EDGE,{"derivedFrom":subQ2}),1.0]])]});}
            var Q6;
            {var subQ0=sQuery(id+"F11.wireOp",EDGE,"E208");Q6=makeQuery(id+"F11.imprint","IMPRINT",FACE,{"disambiguationData":[TD([[makeQuery(id+"F11.imprint","IMPRINT",EDGE,{"derivedFrom":subQ0}),-1.0]])]});}
            var Q7;
            Q7=makeQuery(id+"F11.imprint","IMPRINT",FACE,{"disambiguationData":[TD([[makeQuery(id+"F11.imprint","IMPRINT",EDGE,{"derivedFrom":sQuery(id+"F11.wireOp",EDGE,"E216.trimOffspring")}),1.0]])]});
            var Q8;
            Q8=makeQuery(id+"F11.imprint","IMPRINT",FACE,{"disambiguationData":[TD([[makeQuery(id+"F11.imprint","IMPRINT",EDGE,{"derivedFrom":sQuery(id+"F11.wireOp",EDGE,"E214.trimOffspring")}),-1.0]])]});
            var Q9;
            Q9=makeQuery(id+"F11.imprint","IMPRINT",FACE,{"disambiguationData":[TD([[makeQuery(id+"F11.imprint","IMPRINT",EDGE,{"derivedFrom":sQuery(id+"F11.wireOp",EDGE,"E213")}),-1.0]])]});
            var Q10;
            {var subQ1=sQuery(id+"F11.wireOp",EDGE,"E184.trimOffspring");Q10=makeQuery(id+"F11.imprint","IMPRINT",FACE,{"disambiguationData":[TD([[makeQuery(id+"F11.imprint","IMPRINT",EDGE,{"derivedFrom":subQ1}),1.0]])]});}
            var Q11;
            {var subQ3=sQuery(id+"F11.wireOp",EDGE,"E203.trimOffspring");var subQ5=makeQuery(id+"F11.imprint","IMPRINT",VERTEX,{"derivedFrom":subQ3});Q11=makeQuery(id+"F11.imprint","IMPRINT",FACE,{"disambiguationData":[TD([[makeQuery(id+"F11.imprint","IMPRINT",EDGE,{"disambiguationData":[TD([[subQ5,1.0]])],"derivedFrom":subQ3}),1.0]])]});}
            var Q12;
            {var subQ3=sQuery(id+"F11.wireOp",EDGE,"E261");var subQ11=makeQuery(id+"F11.imprint","IMPRINT",VERTEX,{"derivedFrom":subQ3});Q12=makeQuery(id+"F11.imprint","IMPRINT",FACE,{"disambiguationData":[TD([[makeQuery(id+"F11.imprint","IMPRINT",EDGE,{"disambiguationData":[TD([[subQ11,1.0]])],"derivedFrom":subQ3}),1.0]])]});}
            var Q13;
            Q13=makeQuery(id+"F11.imprint","IMPRINT",FACE,{"disambiguationData":[TD([[makeQuery(id+"F11.imprint","IMPRINT",EDGE,{"derivedFrom":sQuery(id+"F11.wireOp",EDGE,"E247")}),1.0]])]});
            var Q14;
            Q14=makeQuery(id+"F11.imprint","IMPRINT",FACE,{"disambiguationData":[TD([[makeQuery(id+"F11.imprint","IMPRINT",EDGE,{"derivedFrom":sQuery(id+"F11.wireOp",EDGE,"E178.top")}),1.0]])]});
            var Q15;
            Q15=makeQuery(id+"F11.imprint","IMPRINT",FACE,{"disambiguationData":[TD([[makeQuery(id+"F11.imprint","IMPRINT",EDGE,{"derivedFrom":sQuery(id+"F11.wireOp",EDGE,"E178.bottom")}),-1.0]])]});
            var Q16;
            {var subQ4=sQuery(id+"F11.wireOp",EDGE,"E177.bottom");Q16=makeQuery(id+"F11.imprint","IMPRINT",FACE,{"disambiguationData":[TD([[makeQuery(id+"F11.imprint","IMPRINT",EDGE,{"derivedFrom":subQ4}),1.0]])]});}
            var Q17;
            {var subQ0=sQuery(id+"F11.wireOp",EDGE,"E261");var subQ1=sQuery(id+"F11.wireOp",EDGE,"E184.trimOffspring");var subQ2=makeQuery(id+"F11.imprint","INTERSECT",VERTEX,{"derivedFrom":[subQ1,subQ0]});Q17=makeQuery(id+"F11.imprint","IMPRINT",FACE,{"disambiguationData":[TD([[makeQuery(id+"F11.imprint","IMPRINT",EDGE,{"disambiguationData":[TD([[subQ2,-1.0]])],"derivedFrom":subQ1}),1.0]])]});}
            var Q18;
            {var subQ0=sQuery(id+"F11.wireOp",EDGE,"E260.trimOffspring");var subQ4=makeQuery(id+"F11.imprint","IMPRINT",VERTEX,{"derivedFrom":subQ0});Q18=makeQuery(id+"F11.imprint","IMPRINT",FACE,{"disambiguationData":[TD([[makeQuery(id+"F11.imprint","IMPRINT",EDGE,{"disambiguationData":[TD([[subQ4,1.0]])],"derivedFrom":subQ0}),-1.0]])]});}
            extrude(context, id + "F12", {"entities" : qUnion([Q0, Q1, Q2, Q3, Q4, Q5, Q6, Q7, Q8, Q9, Q10, Q11, Q12, Q13, Q14, Q15, Q16, Q17, Q18]), "operationType" : NewBodyOperationType.REMOVE, "endBound" : BoundingType.THROUGH_ALL, "oppositeDirection" : true, "depth" : 25 * mm});
        }
        {
            var Q0;
            {var subQ0=sQuery(id+"F0.wireOp",EDGE,"E12.bottom");Q0=makeQuery(id+"F8.boolean.opBoolean","INTERSECT",EDGE,{"derivedFrom":[makeQuery(id+"F6.boolean.opBoolean","MERGE",FACE,{"derivedFrom":[makeQuery(id+"F1.opExtrude","SWEPT_FACE",FACE,{"disambiguationData":[OSD([subQ0])]}),makeQuery(id+"F6.opExtrude","SWEPT_FACE",FACE,{"disambiguationData":[OSD([subQ0])]})]}),makeQuery(id+"F8.opExtrude","SWEPT_FACE",FACE,{"disambiguationData":[OSD([sQuery(id+"F7.wireOp",EDGE,"E88.top")])]})]});}
            var Q1;
            Q1=makeQuery(id+"F6.opExtrude","CAP_EDGE",EDGE,{"disambiguationData":[OSD([sQuery(id+"F0.wireOp",EDGE,"E12.bottom")])],"isStart":false});
            var Q2;
            Q2=makeQuery(id+"F6.opExtrude","CAP_EDGE",EDGE,{"disambiguationData":[OSD([sQuery(id+"F0.wireOp",EDGE,"E81.trimOffspring")])],"isStart":false});
            var Q3;
            Q3=makeQuery(id+"F6.opExtrude","CAP_EDGE",EDGE,{"disambiguationData":[OSD([sQuery(id+"F0.wireOp",EDGE,"E34.bottom"),sQuery(id+"F0.wireOp",EDGE,"E78")])],"isStart":false});
            var Q4;
            {var subQ0=sQuery(id+"F0.wireOp",EDGE,"E78");var subQ1=sQuery(id+"F0.wireOp",EDGE,"E34.bottom");Q4=makeQuery(id+"F8.boolean.opBoolean","INTERSECT",EDGE,{"derivedFrom":[makeQuery(id+"F6.boolean.opBoolean","MERGE",FACE,{"derivedFrom":[makeQuery(id+"F1.opExtrude","SWEPT_FACE",FACE,{"disambiguationData":[OSD([subQ1,subQ0])]}),makeQuery(id+"F6.opExtrude","SWEPT_FACE",FACE,{"disambiguationData":[OSD([subQ1,subQ0])]})]}),makeQuery(id+"F8.opExtrude","SWEPT_FACE",FACE,{"disambiguationData":[OSD([sQuery(id+"F7.wireOp",EDGE,"E88.top")])]})]});}
            var Q5;
            {var subQ0=sQuery(id+"F0.wireOp",EDGE,"E78");var subQ1=sQuery(id+"F0.wireOp",EDGE,"E34.bottom");Q5=makeQuery(id+"F8.boolean.opBoolean","INTERSECT",EDGE,{"derivedFrom":[makeQuery(id+"F6.boolean.opBoolean","MERGE",FACE,{"derivedFrom":[makeQuery(id+"F1.opExtrude","SWEPT_FACE",FACE,{"disambiguationData":[OSD([subQ1,subQ0])]}),makeQuery(id+"F6.opExtrude","SWEPT_FACE",FACE,{"disambiguationData":[OSD([subQ1,subQ0])]})]}),makeQuery(id+"F8.opExtrude","SWEPT_FACE",FACE,{"disambiguationData":[OSD([sQuery(id+"F7.wireOp",EDGE,"E91.bottom")])]})]});}
            var Q6;
            {var subQ0=sQuery(id+"F0.wireOp",EDGE,"E78");var subQ1=sQuery(id+"F0.wireOp",EDGE,"E34.bottom");Q6=makeQuery(id+"F8.boolean.opBoolean","INTERSECT",EDGE,{"derivedFrom":[makeQuery(id+"F6.boolean.opBoolean","MERGE",FACE,{"derivedFrom":[makeQuery(id+"F1.opExtrude","SWEPT_FACE",FACE,{"disambiguationData":[OSD([subQ1,subQ0])]}),makeQuery(id+"F6.opExtrude","SWEPT_FACE",FACE,{"disambiguationData":[OSD([subQ1,subQ0])]})]}),makeQuery(id+"F8.opExtrude","SWEPT_FACE",FACE,{"disambiguationData":[OSD([sQuery(id+"F7.wireOp",EDGE,"E91.top")])]})]});}
            var Q7;
            {var subQ0=sQuery(id+"F0.wireOp",EDGE,"E81.trimOffspring");Q7=makeQuery(id+"F8.boolean.opBoolean","INTERSECT",EDGE,{"derivedFrom":[makeQuery(id+"F6.boolean.opBoolean","MERGE",FACE,{"derivedFrom":[makeQuery(id+"F1.opExtrude","SWEPT_FACE",FACE,{"disambiguationData":[OSD([subQ0])]}),makeQuery(id+"F6.opExtrude","SWEPT_FACE",FACE,{"disambiguationData":[OSD([subQ0])]})]}),makeQuery(id+"F8.opExtrude","SWEPT_FACE",FACE,{"disambiguationData":[OSD([sQuery(id+"F7.wireOp",EDGE,"E91.top")])]})]});}
            var Q8;
            {var subQ0=sQuery(id+"F0.wireOp",EDGE,"E81.trimOffspring");Q8=makeQuery(id+"F8.boolean.opBoolean","INTERSECT",EDGE,{"derivedFrom":[makeQuery(id+"F6.boolean.opBoolean","MERGE",FACE,{"derivedFrom":[makeQuery(id+"F1.opExtrude","SWEPT_FACE",FACE,{"disambiguationData":[OSD([subQ0])]}),makeQuery(id+"F6.opExtrude","SWEPT_FACE",FACE,{"disambiguationData":[OSD([subQ0])]})]}),makeQuery(id+"F8.opExtrude","SWEPT_FACE",FACE,{"disambiguationData":[OSD([sQuery(id+"F7.wireOp",EDGE,"E91.bottom")])]})]});}
            var Q9;
            {var subQ0=sQuery(id+"F0.wireOp",EDGE,"E81.trimOffspring");Q9=makeQuery(id+"F8.boolean.opBoolean","INTERSECT",EDGE,{"derivedFrom":[makeQuery(id+"F6.boolean.opBoolean","MERGE",FACE,{"derivedFrom":[makeQuery(id+"F1.opExtrude","SWEPT_FACE",FACE,{"disambiguationData":[OSD([subQ0])]}),makeQuery(id+"F6.opExtrude","SWEPT_FACE",FACE,{"disambiguationData":[OSD([subQ0])]})]}),makeQuery(id+"F8.opExtrude","SWEPT_FACE",FACE,{"disambiguationData":[OSD([sQuery(id+"F7.wireOp",EDGE,"E88.top")])]})]});}
            var Q10;
            {var subQ0=sQuery(id+"F0.wireOp",EDGE,"E78");var subQ1=sQuery(id+"F0.wireOp",EDGE,"E34.bottom");Q10=makeQuery(id+"F8.boolean.opBoolean","INTERSECT",EDGE,{"derivedFrom":[makeQuery(id+"F6.boolean.opBoolean","MERGE",FACE,{"derivedFrom":[makeQuery(id+"F1.opExtrude","SWEPT_FACE",FACE,{"disambiguationData":[OSD([subQ1,subQ0])]}),makeQuery(id+"F6.opExtrude","SWEPT_FACE",FACE,{"disambiguationData":[OSD([subQ1,subQ0])]})]}),makeQuery(id+"F8.opExtrude","SWEPT_FACE",FACE,{"disambiguationData":[OSD([sQuery(id+"F7.wireOp",EDGE,"E89.top")])]})]});}
            var Q11;
            Q11=makeQuery(id+"F1.opExtrude","CAP_EDGE",EDGE,{"disambiguationData":[OSD([sQuery(id+"F0.wireOp",EDGE,"E34.bottom"),sQuery(id+"F0.wireOp",EDGE,"E78")])],"isStart":true});
            var Q12;
            Q12=makeQuery(id+"F1.opExtrude","CAP_EDGE",EDGE,{"disambiguationData":[OSD([sQuery(id+"F0.wireOp",EDGE,"E81.trimOffspring")])],"isStart":true});
            var Q13;
            {var subQ0=sQuery(id+"F0.wireOp",EDGE,"E81.trimOffspring");Q13=makeQuery(id+"F8.boolean.opBoolean","INTERSECT",EDGE,{"derivedFrom":[makeQuery(id+"F6.boolean.opBoolean","MERGE",FACE,{"derivedFrom":[makeQuery(id+"F1.opExtrude","SWEPT_FACE",FACE,{"disambiguationData":[OSD([subQ0])]}),makeQuery(id+"F6.opExtrude","SWEPT_FACE",FACE,{"disambiguationData":[OSD([subQ0])]})]}),makeQuery(id+"F8.opExtrude","SWEPT_FACE",FACE,{"disambiguationData":[OSD([sQuery(id+"F7.wireOp",EDGE,"E89.top")])]})]});}
            var Q14;
            {var subQ0=sQuery(id+"F0.wireOp",EDGE,"E12.bottom");Q14=makeQuery(id+"F8.boolean.opBoolean","INTERSECT",EDGE,{"derivedFrom":[makeQuery(id+"F6.boolean.opBoolean","MERGE",FACE,{"derivedFrom":[makeQuery(id+"F1.opExtrude","SWEPT_FACE",FACE,{"disambiguationData":[OSD([subQ0])]}),makeQuery(id+"F6.opExtrude","SWEPT_FACE",FACE,{"disambiguationData":[OSD([subQ0])]})]}),makeQuery(id+"F8.opExtrude","SWEPT_FACE",FACE,{"disambiguationData":[OSD([sQuery(id+"F7.wireOp",EDGE,"E89.top")])]})]});}
            var Q15;
            Q15=makeQuery(id+"F6.opExtrude","CAP_EDGE",EDGE,{"disambiguationData":[OSD([sQuery(id+"F0.wireOp",EDGE,"E12.bottom")])],"isStart":true});
            var Q16;
            {var subQ0=sQuery(id+"F0.wireOp",EDGE,"E12.bottom");Q16=makeQuery(id+"F8.boolean.opBoolean","INTERSECT",EDGE,{"derivedFrom":[makeQuery(id+"F6.boolean.opBoolean","MERGE",FACE,{"derivedFrom":[makeQuery(id+"F1.opExtrude","SWEPT_FACE",FACE,{"disambiguationData":[OSD([subQ0])]}),makeQuery(id+"F6.opExtrude","SWEPT_FACE",FACE,{"disambiguationData":[OSD([subQ0])]})]}),makeQuery(id+"F8.opExtrude","SWEPT_FACE",FACE,{"disambiguationData":[OSD([sQuery(id+"F7.wireOp",EDGE,"E91.top")])]})]});}
            var Q17;
            {var subQ0=sQuery(id+"F0.wireOp",EDGE,"E12.bottom");Q17=makeQuery(id+"F8.boolean.opBoolean","INTERSECT",EDGE,{"derivedFrom":[makeQuery(id+"F6.boolean.opBoolean","MERGE",FACE,{"derivedFrom":[makeQuery(id+"F1.opExtrude","SWEPT_FACE",FACE,{"disambiguationData":[OSD([subQ0])]}),makeQuery(id+"F6.opExtrude","SWEPT_FACE",FACE,{"disambiguationData":[OSD([subQ0])]})]}),makeQuery(id+"F8.opExtrude","SWEPT_FACE",FACE,{"disambiguationData":[OSD([sQuery(id+"F7.wireOp",EDGE,"E91.bottom")])]})]});}
            var Q18;
            {var subQ0=sQuery(id+"F0.wireOp",EDGE,"E14");Q18=makeQuery(id+"F8.boolean.opBoolean","INTERSECT",EDGE,{"derivedFrom":[makeQuery(id+"F6.boolean.opBoolean","MERGE",FACE,{"derivedFrom":[makeQuery(id+"F1.opExtrude","SWEPT_FACE",FACE,{"disambiguationData":[OSD([subQ0])]}),makeQuery(id+"F6.opExtrude","SWEPT_FACE",FACE,{"disambiguationData":[OSD([subQ0])]})]}),makeQuery(id+"F8.opExtrude","SWEPT_FACE",FACE,{"disambiguationData":[OSD([sQuery(id+"F7.wireOp",EDGE,"E91.bottom")])]})]});}
            var Q19;
            {var subQ0=sQuery(id+"F0.wireOp",EDGE,"E14");Q19=makeQuery(id+"F8.boolean.opBoolean","INTERSECT",EDGE,{"derivedFrom":[makeQuery(id+"F6.boolean.opBoolean","MERGE",FACE,{"derivedFrom":[makeQuery(id+"F1.opExtrude","SWEPT_FACE",FACE,{"disambiguationData":[OSD([subQ0])]}),makeQuery(id+"F6.opExtrude","SWEPT_FACE",FACE,{"disambiguationData":[OSD([subQ0])]})]}),makeQuery(id+"F8.opExtrude","SWEPT_FACE",FACE,{"disambiguationData":[OSD([sQuery(id+"F7.wireOp",EDGE,"E91.top")])]})]});}
            var Q20;
            {var subQ0=sQuery(id+"F0.wireOp",EDGE,"E14");Q20=makeQuery(id+"F8.boolean.opBoolean","INTERSECT",EDGE,{"derivedFrom":[makeQuery(id+"F6.boolean.opBoolean","MERGE",FACE,{"derivedFrom":[makeQuery(id+"F1.opExtrude","SWEPT_FACE",FACE,{"disambiguationData":[OSD([subQ0])]}),makeQuery(id+"F6.opExtrude","SWEPT_FACE",FACE,{"disambiguationData":[OSD([subQ0])]})]}),makeQuery(id+"F8.opExtrude","SWEPT_FACE",FACE,{"disambiguationData":[OSD([sQuery(id+"F7.wireOp",EDGE,"E88.top")])]})]});}
            var Q21;
            Q21=makeQuery(id+"F6.opExtrude","CAP_EDGE",EDGE,{"disambiguationData":[OSD([sQuery(id+"F0.wireOp",EDGE,"E14")])],"isStart":false});
            var Q22;
            {var subQ0=sQuery(id+"F0.wireOp",EDGE,"E14");Q22=makeQuery(id+"F8.boolean.opBoolean","INTERSECT",EDGE,{"derivedFrom":[makeQuery(id+"F6.boolean.opBoolean","MERGE",FACE,{"derivedFrom":[makeQuery(id+"F1.opExtrude","SWEPT_FACE",FACE,{"disambiguationData":[OSD([subQ0])]}),makeQuery(id+"F6.opExtrude","SWEPT_FACE",FACE,{"disambiguationData":[OSD([subQ0])]})]}),makeQuery(id+"F8.opExtrude","SWEPT_FACE",FACE,{"disambiguationData":[OSD([sQuery(id+"F7.wireOp",EDGE,"E89.top")])]})]});}
            var Q23;
            Q23=makeQuery(id+"F6.opExtrude","CAP_EDGE",EDGE,{"disambiguationData":[OSD([sQuery(id+"F0.wireOp",EDGE,"E14")])],"isStart":true});
            var Q24;
            Q24=makeQuery(id+"F1.opExtrude","CAP_EDGE",EDGE,{"disambiguationData":[OSD([sQuery(id+"F0.wireOp",EDGE,"E19.top")])],"isStart":true});
            var Q25;
            {var subQ0=sQuery(id+"F0.wireOp",EDGE,"E19.top");Q25=makeQuery(id+"F8.boolean.opBoolean","INTERSECT",EDGE,{"derivedFrom":[makeQuery(id+"F6.boolean.opBoolean","MERGE",FACE,{"derivedFrom":[makeQuery(id+"F1.opExtrude","SWEPT_FACE",FACE,{"disambiguationData":[OSD([subQ0])]}),makeQuery(id+"F6.opExtrude","SWEPT_FACE",FACE,{"disambiguationData":[OSD([subQ0])]})]}),makeQuery(id+"F8.opExtrude","SWEPT_FACE",FACE,{"disambiguationData":[OSD([sQuery(id+"F7.wireOp",EDGE,"E89.top")])]})]});}
            var Q26;
            {var subQ0=sQuery(id+"F0.wireOp",EDGE,"E19.top");Q26=makeQuery(id+"F8.boolean.opBoolean","INTERSECT",EDGE,{"derivedFrom":[makeQuery(id+"F6.boolean.opBoolean","MERGE",FACE,{"derivedFrom":[makeQuery(id+"F1.opExtrude","SWEPT_FACE",FACE,{"disambiguationData":[OSD([subQ0])]}),makeQuery(id+"F6.opExtrude","SWEPT_FACE",FACE,{"disambiguationData":[OSD([subQ0])]})]}),makeQuery(id+"F8.opExtrude","SWEPT_FACE",FACE,{"disambiguationData":[OSD([sQuery(id+"F7.wireOp",EDGE,"E91.top")])]})]});}
            var Q27;
            {var subQ0=sQuery(id+"F0.wireOp",EDGE,"E19.top");Q27=makeQuery(id+"F8.boolean.opBoolean","INTERSECT",EDGE,{"derivedFrom":[makeQuery(id+"F6.boolean.opBoolean","MERGE",FACE,{"derivedFrom":[makeQuery(id+"F1.opExtrude","SWEPT_FACE",FACE,{"disambiguationData":[OSD([subQ0])]}),makeQuery(id+"F6.opExtrude","SWEPT_FACE",FACE,{"disambiguationData":[OSD([subQ0])]})]}),makeQuery(id+"F8.opExtrude","SWEPT_FACE",FACE,{"disambiguationData":[OSD([sQuery(id+"F7.wireOp",EDGE,"E91.bottom")])]})]});}
            var Q28;
            {var subQ0=sQuery(id+"F0.wireOp",EDGE,"E19.top");Q28=makeQuery(id+"F8.boolean.opBoolean","INTERSECT",EDGE,{"derivedFrom":[makeQuery(id+"F6.boolean.opBoolean","MERGE",FACE,{"derivedFrom":[makeQuery(id+"F1.opExtrude","SWEPT_FACE",FACE,{"disambiguationData":[OSD([subQ0])]}),makeQuery(id+"F6.opExtrude","SWEPT_FACE",FACE,{"disambiguationData":[OSD([subQ0])]})]}),makeQuery(id+"F8.opExtrude","SWEPT_FACE",FACE,{"disambiguationData":[OSD([sQuery(id+"F7.wireOp",EDGE,"E88.top")])]})]});}
            var Q29;
            Q29=makeQuery(id+"F6.opExtrude","CAP_EDGE",EDGE,{"disambiguationData":[OSD([sQuery(id+"F0.wireOp",EDGE,"E19.top")])],"isStart":false});
            var Q30;
            Q30=makeQuery(id+"F6.opExtrude","CAP_EDGE",EDGE,{"disambiguationData":[OSD([sQuery(id+"F0.wireOp",EDGE,"E76")])],"isStart":false});
            var Q31;
            Q31=makeQuery(id+"F8.boolean.opBoolean","COPY",EDGE,{"derivedFrom":makeQuery(id+"F8.opExtrude","CAP_EDGE",EDGE,{"disambiguationData":[OSD([sQuery(id+"F7.wireOp",EDGE,"E88.top")])],"isStart":true})});
            var Q32;
            Q32=makeQuery(id+"F8.boolean.opBoolean","COPY",EDGE,{"derivedFrom":makeQuery(id+"F8.opExtrude","CAP_EDGE",EDGE,{"disambiguationData":[OSD([sQuery(id+"F7.wireOp",EDGE,"E91.bottom")])],"isStart":true})});
            var Q33;
            Q33=makeQuery(id+"F8.boolean.opBoolean","COPY",EDGE,{"derivedFrom":makeQuery(id+"F8.opExtrude","CAP_EDGE",EDGE,{"disambiguationData":[OSD([sQuery(id+"F7.wireOp",EDGE,"E91.top")])],"isStart":true})});
            var Q34;
            Q34=makeQuery(id+"F8.boolean.opBoolean","COPY",EDGE,{"derivedFrom":makeQuery(id+"F8.opExtrude","CAP_EDGE",EDGE,{"disambiguationData":[OSD([sQuery(id+"F7.wireOp",EDGE,"E89.top")])],"isStart":true})});
            var Q35;
            Q35=makeQuery(id+"F1.opExtrude","CAP_EDGE",EDGE,{"disambiguationData":[OSD([sQuery(id+"F0.wireOp",EDGE,"E76")])],"isStart":true});
            var Q36;
            {var subQ0=sQuery(id+"F0.wireOp",EDGE,"E5");Q36=makeQuery(id+"F8.boolean.opBoolean","INTERSECT",EDGE,{"derivedFrom":[makeQuery(id+"F6.boolean.opBoolean","MERGE",FACE,{"derivedFrom":[makeQuery(id+"F1.opExtrude","SWEPT_FACE",FACE,{"disambiguationData":[OSD([subQ0])]}),makeQuery(id+"F6.opExtrude","SWEPT_FACE",FACE,{"disambiguationData":[OSD([subQ0])]})]}),makeQuery(id+"F8.opExtrude","SWEPT_FACE",FACE,{"disambiguationData":[OSD([sQuery(id+"F7.wireOp",EDGE,"E91.top")])]})]});}
            var Q37;
            {var subQ0=sQuery(id+"F0.wireOp",EDGE,"E5");Q37=makeQuery(id+"F8.boolean.opBoolean","INTERSECT",EDGE,{"derivedFrom":[makeQuery(id+"F6.boolean.opBoolean","MERGE",FACE,{"derivedFrom":[makeQuery(id+"F1.opExtrude","SWEPT_FACE",FACE,{"disambiguationData":[OSD([subQ0])]}),makeQuery(id+"F6.opExtrude","SWEPT_FACE",FACE,{"disambiguationData":[OSD([subQ0])]})]}),makeQuery(id+"F8.opExtrude","SWEPT_FACE",FACE,{"disambiguationData":[OSD([sQuery(id+"F7.wireOp",EDGE,"E91.bottom")])]})]});}
            var Q38;
            {var subQ0=sQuery(id+"F0.wireOp",EDGE,"E5");Q38=makeQuery(id+"F8.boolean.opBoolean","INTERSECT",EDGE,{"derivedFrom":[makeQuery(id+"F6.boolean.opBoolean","MERGE",FACE,{"derivedFrom":[makeQuery(id+"F1.opExtrude","SWEPT_FACE",FACE,{"disambiguationData":[OSD([subQ0])]}),makeQuery(id+"F6.opExtrude","SWEPT_FACE",FACE,{"disambiguationData":[OSD([subQ0])]})]}),makeQuery(id+"F8.opExtrude","SWEPT_FACE",FACE,{"disambiguationData":[OSD([sQuery(id+"F7.wireOp",EDGE,"E89.top")])]})]});}
            var Q39;
            Q39=makeQuery(id+"F6.opExtrude","CAP_EDGE",EDGE,{"disambiguationData":[OSD([sQuery(id+"F0.wireOp",EDGE,"E5")])],"isStart":true});
            var Q40;
            {var subQ0=sQuery(id+"F0.wireOp",EDGE,"E5");Q40=makeQuery(id+"F8.boolean.opBoolean","INTERSECT",EDGE,{"derivedFrom":[makeQuery(id+"F6.boolean.opBoolean","MERGE",FACE,{"derivedFrom":[makeQuery(id+"F1.opExtrude","SWEPT_FACE",FACE,{"disambiguationData":[OSD([subQ0])]}),makeQuery(id+"F6.opExtrude","SWEPT_FACE",FACE,{"disambiguationData":[OSD([subQ0])]})]}),makeQuery(id+"F8.opExtrude","SWEPT_FACE",FACE,{"disambiguationData":[OSD([sQuery(id+"F7.wireOp",EDGE,"E88.top")])]})]});}
            var Q41;
            Q41=makeQuery(id+"F6.opExtrude","CAP_EDGE",EDGE,{"disambiguationData":[OSD([sQuery(id+"F0.wireOp",EDGE,"E5")])],"isStart":false});
            fillet(context, id + "F13", {"entities" : qUnion([Q0, Q1, Q2, Q3, Q4, Q5, Q6, Q7, Q8, Q9, Q10, Q11, Q12, Q13, Q14, Q15, Q16, Q17, Q18, Q19, Q20, Q21, Q22, Q23, Q24, Q25, Q26, Q27, Q28, Q29, Q30, Q31, Q32, Q33, Q34, Q35, Q36, Q37, Q38, Q39, Q40, Q41]), "radius" : 2 * mm, "tangentPropagation" : true, "allowEdgeOverflow" : false});
        }
        {
            var Q0;
            {var subQ0=sQuery(id+"F0.wireOp",EDGE,"E3");Q0=makeQuery(id+"F8.boolean.opBoolean","INTERSECT",EDGE,{"derivedFrom":[makeQuery(id+"F6.boolean.opBoolean","MERGE",FACE,{"derivedFrom":[makeQuery(id+"F1.opExtrude","SWEPT_FACE",FACE,{"disambiguationData":[OSD([subQ0])]}),makeQuery(id+"F6.opExtrude","SWEPT_FACE",FACE,{"disambiguationData":[OSD([subQ0])]})]}),makeQuery(id+"F8.opExtrude","SWEPT_FACE",FACE,{"disambiguationData":[OSD([sQuery(id+"F7.wireOp",EDGE,"E91.bottom")])]})]});}
            var Q1;
            {var subQ0=sQuery(id+"F0.wireOp",EDGE,"E3");Q1=makeQuery(id+"F8.boolean.opBoolean","INTERSECT",EDGE,{"derivedFrom":[makeQuery(id+"F6.boolean.opBoolean","MERGE",FACE,{"derivedFrom":[makeQuery(id+"F1.opExtrude","SWEPT_FACE",FACE,{"disambiguationData":[OSD([subQ0])]}),makeQuery(id+"F6.opExtrude","SWEPT_FACE",FACE,{"disambiguationData":[OSD([subQ0])]})]}),makeQuery(id+"F8.opExtrude","SWEPT_FACE",FACE,{"disambiguationData":[OSD([sQuery(id+"F7.wireOp",EDGE,"E89.top")])]})]});}
            var Q2;
            Q2=makeQuery(id+"F6.opExtrude","CAP_EDGE",EDGE,{"disambiguationData":[OSD([sQuery(id+"F0.wireOp",EDGE,"E3")])],"isStart":true});
            var Q3;
            {var subQ0=sQuery(id+"F0.wireOp",EDGE,"E3");Q3=makeQuery(id+"F8.boolean.opBoolean","INTERSECT",EDGE,{"derivedFrom":[makeQuery(id+"F6.boolean.opBoolean","MERGE",FACE,{"derivedFrom":[makeQuery(id+"F1.opExtrude","SWEPT_FACE",FACE,{"disambiguationData":[OSD([subQ0])]}),makeQuery(id+"F6.opExtrude","SWEPT_FACE",FACE,{"disambiguationData":[OSD([subQ0])]})]}),makeQuery(id+"F8.opExtrude","SWEPT_FACE",FACE,{"disambiguationData":[OSD([sQuery(id+"F7.wireOp",EDGE,"E91.top")])]})]});}
            var Q4;
            {var subQ0=sQuery(id+"F0.wireOp",EDGE,"E3");Q4=makeQuery(id+"F8.boolean.opBoolean","INTERSECT",EDGE,{"derivedFrom":[makeQuery(id+"F6.boolean.opBoolean","MERGE",FACE,{"derivedFrom":[makeQuery(id+"F1.opExtrude","SWEPT_FACE",FACE,{"disambiguationData":[OSD([subQ0])]}),makeQuery(id+"F6.opExtrude","SWEPT_FACE",FACE,{"disambiguationData":[OSD([subQ0])]})]}),makeQuery(id+"F8.opExtrude","SWEPT_FACE",FACE,{"disambiguationData":[OSD([sQuery(id+"F7.wireOp",EDGE,"E88.top")])]})]});}
            var Q5;
            Q5=makeQuery(id+"F6.opExtrude","CAP_EDGE",EDGE,{"disambiguationData":[OSD([sQuery(id+"F0.wireOp",EDGE,"E3")])],"isStart":false});
            chamfer(context, id + "F14", {"entities" : qUnion([Q0, Q1, Q2, Q3, Q4, Q5]), "width" : 1 * mm, "tangentPropagation" : true});
        }
        {
            var Q0;
            Q0=makeQuery(id+"F12.boolean.opBoolean","SPLIT",BODY,{"disambiguationData":[OD(0.0)],"derivedFrom":makeQuery(id+"F1.opExtrude","SWEPT_BODY",BODY,{"disambiguationData":[OSD([sQuery(id+"F0.wireOp",EDGE,"E1.bottom"),sQuery(id+"F0.wireOp",EDGE,"E1.top"),sQuery(id+"F0.wireOp",EDGE,"E2"),sQuery(id+"F0.wireOp",EDGE,"E3"),sQuery(id+"F0.wireOp",EDGE,"E4"),sQuery(id+"F0.wireOp",EDGE,"E5"),sQuery(id+"F0.wireOp",EDGE,"E6"),sQuery(id+"F0.wireOp",EDGE,"E7"),sQuery(id+"F0.wireOp",EDGE,"E8.left"),sQuery(id+"F0.wireOp",EDGE,"E8.right"),sQuery(id+"F0.wireOp",EDGE,"E10.left"),sQuery(id+"F0.wireOp",EDGE,"E12.bottom"),sQuery(id+"F0.wireOp",EDGE,"E12.left"),sQuery(id+"F0.wireOp",EDGE,"E13"),sQuery(id+"F0.wireOp",EDGE,"E14"),sQuery(id+"F0.wireOp",EDGE,"E17.left"),sQuery(id+"F0.wireOp",EDGE,"E17.right"),sQuery(id+"F0.wireOp",EDGE,"E18.left"),sQuery(id+"F0.wireOp",EDGE,"E18.right"),sQuery(id+"F0.wireOp",EDGE,"E19.top"),sQuery(id+"F0.wireOp",EDGE,"E20.bottom"),sQuery(id+"F0.wireOp",EDGE,"E20.left"),sQuery(id+"F0.wireOp",EDGE,"E21.left"),sQuery(id+"F0.wireOp",EDGE,"E22.bottom"),sQuery(id+"F0.wireOp",EDGE,"E22.top"),sQuery(id+"F0.wireOp",EDGE,"E25"),sQuery(id+"F0.wireOp",EDGE,"E26"),sQuery(id+"F0.wireOp",EDGE,"E27"),sQuery(id+"F0.wireOp",EDGE,"E28"),sQuery(id+"F0.wireOp",EDGE,"E30"),sQuery(id+"F0.wireOp",EDGE,"E31"),sQuery(id+"F0.wireOp",EDGE,"E32"),sQuery(id+"F0.wireOp",EDGE,"E33"),sQuery(id+"F0.wireOp",EDGE,"E34.bottom"),sQuery(id+"F0.wireOp",EDGE,"E34.top"),sQuery(id+"F0.wireOp",EDGE,"E35"),sQuery(id+"F0.wireOp",EDGE,"E36"),sQuery(id+"F0.wireOp",EDGE,"E38"),sQuery(id+"F0.wireOp",EDGE,"E40.trimOffspring"),sQuery(id+"F0.wireOp",EDGE,"E41"),sQuery(id+"F0.wireOp",EDGE,"E42"),sQuery(id+"F0.wireOp",EDGE,"E43"),sQuery(id+"F0.wireOp",EDGE,"E44"),sQuery(id+"F0.wireOp",EDGE,"E45"),sQuery(id+"F0.wireOp",EDGE,"E46"),sQuery(id+"F0.wireOp",EDGE,"E47"),sQuery(id+"F0.wireOp",EDGE,"E48.trimOffspring"),sQuery(id+"F0.wireOp",EDGE,"E50.trimOffspring"),sQuery(id+"F0.wireOp",EDGE,"E52"),sQuery(id+"F0.wireOp",EDGE,"E54"),sQuery(id+"F0.wireOp",EDGE,"E55.trimOffspring"),sQuery(id+"F0.wireOp",EDGE,"E56"),sQuery(id+"F0.wireOp",EDGE,"E57"),sQuery(id+"F0.wireOp",EDGE,"E58"),sQuery(id+"F0.wireOp",EDGE,"E59"),sQuery(id+"F0.wireOp",EDGE,"E60"),sQuery(id+"F0.wireOp",EDGE,"E61.trimOffspring"),sQuery(id+"F0.wireOp",EDGE,"E62"),sQuery(id+"F0.wireOp",EDGE,"E63"),sQuery(id+"F0.wireOp",EDGE,"E65"),sQuery(id+"F0.wireOp",EDGE,"E66"),sQuery(id+"F0.wireOp",EDGE,"E67.trimOffspring"),sQuery(id+"F0.wireOp",EDGE,"E68"),sQuery(id+"F0.wireOp",EDGE,"E69"),sQuery(id+"F0.wireOp",EDGE,"E70"),sQuery(id+"F0.wireOp",EDGE,"E71"),sQuery(id+"F0.wireOp",EDGE,"E72"),sQuery(id+"F0.wireOp",EDGE,"E73"),sQuery(id+"F0.wireOp",EDGE,"E74.trimOffspring"),sQuery(id+"F0.wireOp",EDGE,"E75"),sQuery(id+"F0.wireOp",EDGE,"E76"),sQuery(id+"F0.wireOp",EDGE,"E77"),sQuery(id+"F0.wireOp",EDGE,"E78"),sQuery(id+"F0.wireOp",EDGE,"E81.trimOffspring"),sQuery(id+"F0.wireOp",EDGE,"E83.trimOffspring"),sQuery(id+"F0.wireOp",EDGE,"E84.trimOffspring"),sQuery(id+"F0.wireOp",EDGE,"E86")])]})});
            transform(context, id + "F15", {"entities" : qUnion([Q0]), "transformType" : TransformType.TRANSLATION_3D, "dx" : 0 * mm, "dy" : 0 * mm, "dz" : 0 * mm, "makeCopy" : true});
        }
    });
